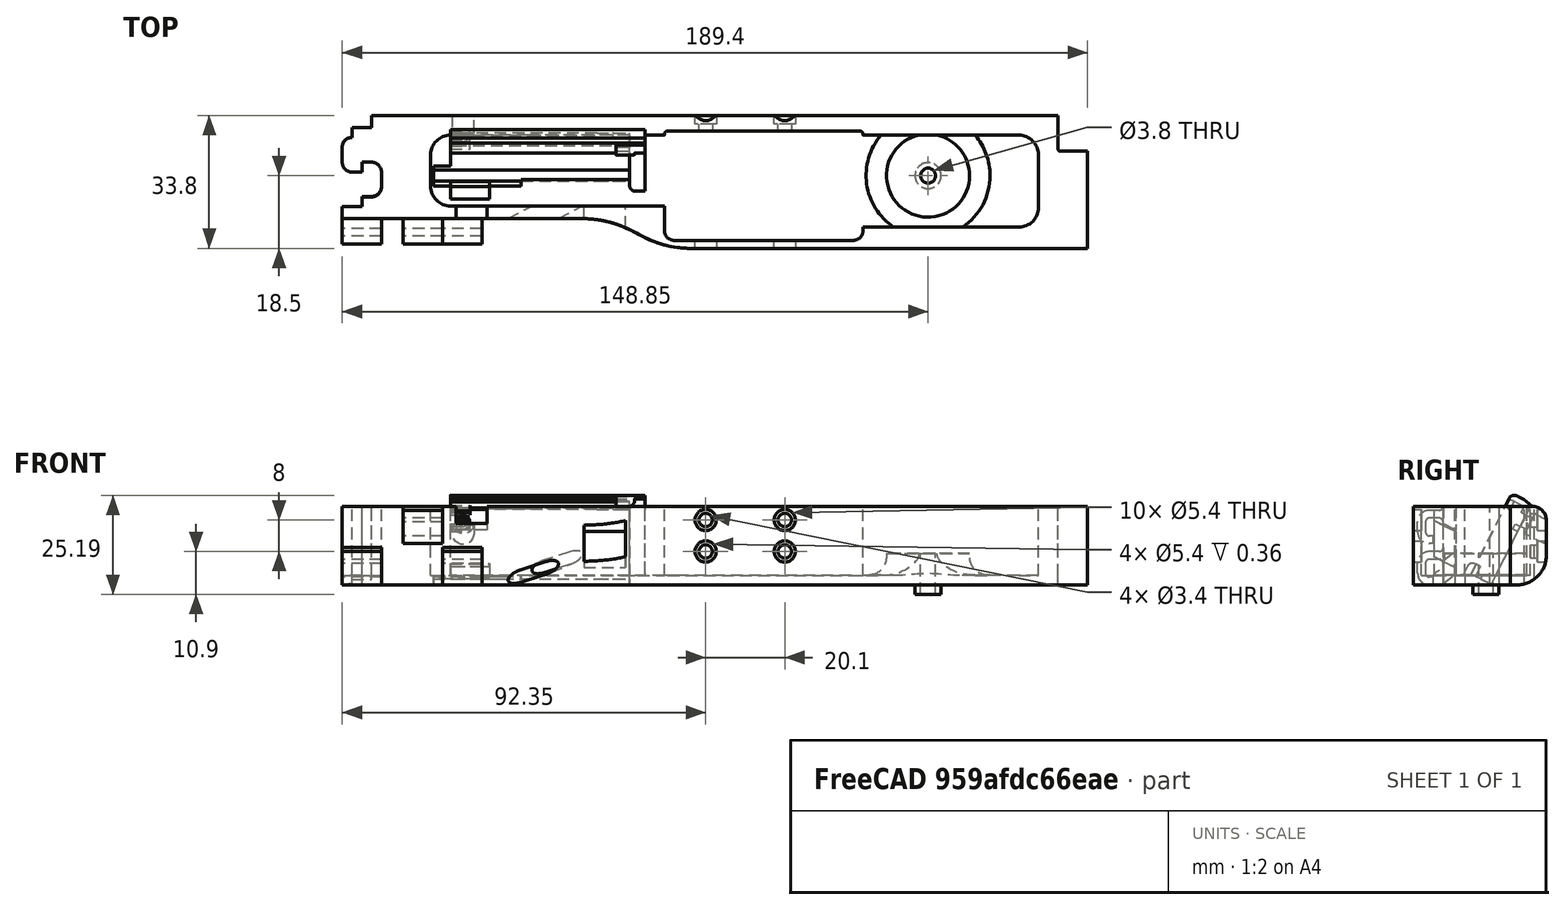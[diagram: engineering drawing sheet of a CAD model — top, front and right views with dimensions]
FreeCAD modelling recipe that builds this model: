
FCSTD DOCUMENT  (FreeCAD 0.19R0.19.2)
Label: v0_999
License: All rights reserved
LicenseURL: http://en.wikipedia.org/wiki/All_rights_reserved
objects: Sketcher::SketchObject×44, Part::Extrusion×34, Part::MultiFuse×19, Part::Cut×15, Part::Box×14, Part::Fillet×11, App::MeasureDistance×5, Part::Cylinder×4, Part::Revolution×1, Mesh::Feature×1
note: 142 computed .brp shape members not serialized (recipe doc carries the construction recipe); baked Part::Feature solids carry a one-line shape summary decoded from their .brp

FEATURE [Sketcher::SketchObject] Sketch
  FullyConstrained = true
  sketch-geometry (36):
    g0: LineSegment StartX=0 StartY=0 StartZ=0 EndX=154.4 EndY=0 EndZ=0
    g1: LineSegment StartX=154.4 StartY=0 StartZ=0 EndX=154.4 EndY=-7.6 EndZ=0
    g2: LineSegment StartX=32.5209 StartY=-26.2 StartZ=0 EndX=-7.5 EndY=-26.2 EndZ=0
    g3-g7: Circle x5 (B-spline internal-alignment scaffolding for g8; pole/knot coordinates omitted)
    g8: BSplineCurve PolesCount=5 KnotsCount=3 Degree=3 IsPeriodic=0
    g9: GeomPoint X=61.85 Y=-33.8 Z=0
    g10: GeomPoint X=47.185 Y=-29.9 Z=0
    g11: GeomPoint X=32.5209 Y=-26.2 Z=0
    g12: Circle CenterX=121.35 CenterY=-14.3 CenterZ=0 NormalX=0 NormalY=0 NormalZ=1 AngleXU=0 Radius=3.25
    g13: LineSegment StartX=-7.5 StartY=-26.2 StartZ=0 EndX=-27.5 EndY=-26.2 EndZ=0
    g14: LineSegment StartX=-20 StartY=0 StartZ=0 EndX=0 EndY=0 EndZ=0
    g15: LineSegment StartX=-25 StartY=-3.1 StartZ=0 EndX=-20 EndY=-3.1 EndZ=0
    g16: LineSegment StartX=-25 StartY=-3.1 StartZ=0 EndX=-25 EndY=-5.6 EndZ=0
    g17: LineSegment StartX=-27.5 StartY=-8.1 StartZ=0 EndX=-27.5 EndY=-11.85 EndZ=0
    g18: ArcOfCircle CenterX=-25 CenterY=-8.1 CenterZ=0 NormalX=0 NormalY=0 NormalZ=1 AngleXU=0 Radius=2.5 StartAngle=1.5708 EndAngle=3.14159
    g19: LineSegment StartX=-25 StartY=-14.35 StartZ=0 EndX=-22.5 EndY=-14.35 EndZ=0
    g20: ArcOfCircle CenterX=-25 CenterY=-11.85 CenterZ=0 NormalX=0 NormalY=0 NormalZ=1 AngleXU=0 Radius=2.5 StartAngle=3.14159 EndAngle=4.71239
    g21: LineSegment StartX=-22.5 StartY=-14.35 StartZ=0 EndX=-22.5 EndY=-11.85 EndZ=0
    g22: LineSegment StartX=-22.5 StartY=-11.85 StartZ=0 EndX=-20 EndY=-11.85 EndZ=0
    g23: ArcOfCircle CenterX=-20 CenterY=-14.35 CenterZ=0 NormalX=0 NormalY=0 NormalZ=1 AngleXU=0 Radius=2.5 StartAngle=8e-16 EndAngle=1.5708
    g24: LineSegment StartX=-17.5 StartY=-14.35 StartZ=0 EndX=-17.5 EndY=-18.1 EndZ=0
    g25: ArcOfCircle CenterX=-20 CenterY=-18.1 CenterZ=0 NormalX=0 NormalY=0 NormalZ=1 AngleXU=0 Radius=2.5 StartAngle=4.71239 EndAngle=6.28319
    g26: LineSegment StartX=-22.5 StartY=-20.6 StartZ=0 EndX=-20 EndY=-20.6 EndZ=0
    g27: LineSegment StartX=-22.5 StartY=-20.6 StartZ=0 EndX=-22.5 EndY=-23.1 EndZ=0
    g28: LineSegment StartX=-27.5 StartY=-23.1 StartZ=0 EndX=-22.5 EndY=-23.1 EndZ=0
    g29: LineSegment StartX=-20 StartY=-3.1 StartZ=0 EndX=-20 EndY=0 EndZ=0
    g30: LineSegment StartX=-27.5 StartY=-23.1 StartZ=0 EndX=-27.5 EndY=-26.2 EndZ=0
    g31: LineSegment StartX=154.4 StartY=-7.6 StartZ=0 EndX=154.4 EndY=-8.6 EndZ=0
    g32: ArcOfCircle CenterX=154.9 CenterY=-8.6 CenterZ=0 NormalX=0 NormalY=0 NormalZ=1 AngleXU=0 Radius=0.5 StartAngle=3.14159 EndAngle=4.71239
    g33: LineSegment StartX=154.9 StartY=-9.1 StartZ=0 EndX=161.9 EndY=-9.1 EndZ=0
    g34: LineSegment StartX=161.9 StartY=-9.1 StartZ=0 EndX=161.9 EndY=-33.8 EndZ=0
    g35: LineSegment StartX=161.9 StartY=-33.8 StartZ=0 EndX=61.85 EndY=-33.8 EndZ=0
  constraints (72):
    c: PointOnObject(g0,g-2)
    c: Horizontal(g0)
    c: Distance(g0) = 154.4
    c: DistanceY(g-1,g0) = 0
    c: Vertical(g1)
    c: Distance(g1) = 7.6
    c: Coincident(g1,g0)
    c: Horizontal(g2)
    c: Block(g2)
    c: Weight(g3) = 1
    c: Coincident(g8,g2)
    c: InternalAlignment(g3-g7 -> g8) x5
    c: InternalAlignment(g9,g8)
    c: InternalAlignment(g10,g8)
    c: InternalAlignment(g11,g8)
    c: Block(g12)
    c: Coincident(g13,g2)
    c: Horizontal(g13)
    c: Distance(g13) = 20
    c: Horizontal(g14)
    c: Distance(g14) = 20
    c: Coincident(g14,g0)
    c: Horizontal(g15)
    c: Vertical(g16)
    c: Coincident(g16,g15)
    c: Vertical(g17)
    c: Coincident(g18,g16)
    c: Block(g18)
    c: Coincident(g17,g18)
    c: Horizontal(g19)
    c: Coincident(g20,g17)
    c: Block(g20)
    c: Block(g19)
    c: Vertical(g21)
    c: Coincident(g21,g19)
    c: Horizontal(g22)
    c: Coincident(g22,g21)
    c: Coincident(g23,g22)
    c: Vertical(g24)
    c: Block(g23)
    c: Coincident(g24,g23)
    c: Coincident(g25,g24)
    c: Block(g25)
    c: Horizontal(g26)
    c: Coincident(g26,g25)
    c: Vertical(g27)
    c: Coincident(g27,g26)
    c: Horizontal(g28)
    c: Coincident(g28,g27)
    c: Block(g15)
    c: Block(g28)
    c: Coincident(g29,g15)
    c: Coincident(g29,g14)
    c: Vertical(g29)
    c: Coincident(g30,g28)
    c: Coincident(g30,g13)
    c: Vertical(g30)
    c: Vertical(g31)
    c: Distance(g31) = 1
    c: Coincident(g31,g1)
    c: Coincident(g32,g31)
    c: Block(g32)
    c: Coincident(g33,g32)
    c: Horizontal(g33)
    c: Coincident(g34,g33)
    c: Vertical(g34)
    c: Block(g34)
    c: Coincident(g35,g34)
    c: Horizontal(g35)
    c: Block(g35)
    c: Coincident(g8,g35)
    c: Block(g8)
FEATURE [Part::Extrusion] Extrude  label="mainBodyBaseExtrude"
  Base = -> Sketch
  Dir = (0,0,1)
  DirMode = 2
  FaceMakerClass = Part::FaceMakerBullseye
  LengthFwd = 2.4
  LengthRev = 0
  Solid = true
  Symmetric = false
FEATURE [Sketcher::SketchObject] Sketch001
  FullyConstrained = true
  sketch-geometry (75):
    g0: ArcOfCircle CenterX=144.4 CenterY=-10 CenterZ=0 NormalX=0 NormalY=0 NormalZ=1 AngleXU=0 Radius=5 StartAngle=4.345e-13 EndAngle=1.5708
    g1: LineSegment StartX=32.5209 StartY=-26.2 StartZ=0 EndX=-7.49911 EndY=-26.2 EndZ=0
    g2: LineSegment StartX=0 StartY=0 StartZ=0 EndX=154.4 EndY=0 EndZ=0
    g3-g7: Circle x5 (B-spline internal-alignment scaffolding for g8; pole/knot coordinates omitted)
    g8: BSplineCurve PolesCount=5 KnotsCount=3 Degree=3 IsPeriodic=0
    g9: GeomPoint X=61.85 Y=-33.8 Z=0
    g10: GeomPoint X=47.1857 Y=-29.9 Z=0
    g11: GeomPoint X=32.5209 Y=-26.2 Z=0
    g12: LineSegment StartX=154.4 StartY=0 StartZ=0 EndX=154.4 EndY=-7.6 EndZ=0
    g13: LineSegment StartX=20 StartY=-5 StartZ=0 EndX=54.35 EndY=-5 EndZ=0
    g14: LineSegment StartX=104.85 StartY=-5 StartZ=0 EndX=144.4 EndY=-5 EndZ=0
    g15: LineSegment StartX=54.35 StartY=-23 StartZ=0 EndX=20 EndY=-23 EndZ=0
    g16: LineSegment StartX=-27.4991 StartY=-26.2 StartZ=0 EndX=-7.49911 EndY=-26.2 EndZ=0
    g17: LineSegment StartX=-20 StartY=0 StartZ=0 EndX=0 EndY=0 EndZ=0
    g18: LineSegment StartX=-27.4991 StartY=-23.2 StartZ=0 EndX=-22.5 EndY=-23.2 EndZ=0
    g19: LineSegment StartX=-22.5 StartY=-20.7 StartZ=0 EndX=-22.5 EndY=-23.2 EndZ=0
    g20: LineSegment StartX=-22.5 StartY=-20.7 StartZ=0 EndX=-20 EndY=-20.7 EndZ=0
    g21: ArcOfCircle CenterX=-20 CenterY=-18.2 CenterZ=0 NormalX=0 NormalY=0 NormalZ=1 AngleXU=0 Radius=2.5 StartAngle=4.71239 EndAngle=6.28319
    g22: LineSegment StartX=-17.5 StartY=-14.4 StartZ=0 EndX=-17.5 EndY=-18.2 EndZ=0
    g23: ArcOfCircle CenterX=-20 CenterY=-14.4 CenterZ=0 NormalX=0 NormalY=0 NormalZ=1 AngleXU=0 Radius=2.5 StartAngle=9e-16 EndAngle=1.5708
    g24: LineSegment StartX=-22.5 StartY=-11.9 StartZ=0 EndX=-20 EndY=-11.9 EndZ=0
    g25: LineSegment StartX=-22.5 StartY=-14.4 StartZ=0 EndX=-22.5 EndY=-11.9 EndZ=0
    g26: LineSegment StartX=-25 StartY=-14.4 StartZ=0 EndX=-22.5 EndY=-14.4 EndZ=0
    g27: ArcOfCircle CenterX=-25 CenterY=-11.9 CenterZ=0 NormalX=0 NormalY=0 NormalZ=1 AngleXU=0 Radius=2.5 StartAngle=3.14159 EndAngle=4.71239
    g28: LineSegment StartX=-27.5 StartY=-8.1 StartZ=0 EndX=-27.5 EndY=-11.9 EndZ=0
    g29: ArcOfCircle CenterX=-25 CenterY=-8.1 CenterZ=0 NormalX=0 NormalY=0 NormalZ=1 AngleXU=0 Radius=2.5 StartAngle=1.5708 EndAngle=3.14159
    g30: LineSegment StartX=-25 StartY=-3.1 StartZ=0 EndX=-25 EndY=-5.6 EndZ=0
    g31: LineSegment StartX=-20 StartY=-3.1 StartZ=0 EndX=-25 EndY=-3.1 EndZ=0
    g32: LineSegment StartX=-20 StartY=0 StartZ=0 EndX=-20 EndY=-3.1 EndZ=0
    g33: LineSegment StartX=-27.4991 StartY=-26.2 StartZ=0 EndX=-27.4991 EndY=-23.2 EndZ=0
    g34: LineSegment StartX=4.09e-14 StartY=-5 StartZ=0 EndX=20 EndY=-5 EndZ=0
    g35: ArcOfCircle CenterX=7.1e-15 CenterY=-18 CenterZ=0 NormalX=0 NormalY=0 NormalZ=1 AngleXU=0 Radius=5 StartAngle=3.14159 EndAngle=4.71239
    g36: ArcOfCircle CenterX=4.26e-14 CenterY=-10 CenterZ=0 NormalX=0 NormalY=0 NormalZ=1 AngleXU=0 Radius=5 StartAngle=1.5708 EndAngle=3.14159
    g37: LineSegment StartX=-5 StartY=-18 StartZ=0 EndX=-5 EndY=-10 EndZ=0
    g38: LineSegment StartX=6.2e-15 StartY=-23 StartZ=0 EndX=20 EndY=-23 EndZ=0
    g39: LineSegment StartX=154.4 StartY=-7.6 StartZ=0 EndX=154.4 EndY=-8.6 EndZ=0
    g40: LineSegment StartX=154.9 StartY=-9.1 StartZ=0 EndX=161.9 EndY=-9.1 EndZ=0
    g41: ArcOfCircle CenterX=154.9 CenterY=-8.6 CenterZ=0 NormalX=0 NormalY=0 NormalZ=1 AngleXU=0 Radius=0.5 StartAngle=3.14159 EndAngle=4.71299
    g42: LineSegment StartX=104.85 StartY=-28.3916 StartZ=0 EndX=144.408 EndY=-28.3916 EndZ=0
    g43: LineSegment StartX=149.4 StartY=-10 StartZ=0 EndX=149.4 EndY=-23.4 EndZ=0
    g44: ArcOfCircle CenterX=144.408 CenterY=-23.4 CenterZ=0 NormalX=0 NormalY=0 NormalZ=1 AngleXU=0 Radius=4.99164 StartAngle=4.71239 EndAngle=6.28319
    g45: LineSegment StartX=104.85 StartY=-28.3916 StartZ=0 EndX=104.85 EndY=-28.7833 EndZ=0
    g46: LineSegment StartX=54.35 StartY=-28.7916 StartZ=0 EndX=54.35 EndY=-23 EndZ=0
    g47: LineSegment StartX=161.9 StartY=-33.8 StartZ=0 EndX=161.9 EndY=-9.1 EndZ=0
    g48: LineSegment StartX=61.85 StartY=-33.8 StartZ=0 EndX=161.9 EndY=-33.8 EndZ=0
    g49: Circle CenterX=54.35 CenterY=-28.7916 CenterZ=0 NormalX=0 NormalY=0 NormalZ=1 AngleXU=0 Radius=1
    g50: Circle CenterX=54.35 CenterY=-31.7916 CenterZ=0 NormalX=0 NormalY=0 NormalZ=1 AngleXU=0 Radius=1
    g51: Circle CenterX=57.35 CenterY=-31.7916 CenterZ=0 NormalX=0 NormalY=0 NormalZ=1 AngleXU=0 Radius=1
    g52: BSplineCurve PolesCount=3 KnotsCount=2 Degree=2 IsPeriodic=0
    g53: GeomPoint X=54.35 Y=-28.7916 Z=0
    g54: GeomPoint X=57.35 Y=-31.7916 Z=0
    g55: Circle CenterX=104.85 CenterY=-28.7833 CenterZ=0 NormalX=0 NormalY=0 NormalZ=1 AngleXU=0 Radius=1
    g56: Circle CenterX=104.85 CenterY=-31.7916 CenterZ=0 NormalX=0 NormalY=0 NormalZ=1 AngleXU=0 Radius=1
    g57: Circle CenterX=101.85 CenterY=-31.7916 CenterZ=0 NormalX=0 NormalY=0 NormalZ=1 AngleXU=0 Radius=1
    g58: BSplineCurve PolesCount=3 KnotsCount=2 Degree=2 IsPeriodic=0
    g59: GeomPoint X=104.85 Y=-28.7833 Z=0
    g60: GeomPoint X=101.85 Y=-31.7916 Z=0
    g61: LineSegment StartX=57.35 StartY=-31.7916 StartZ=0 EndX=101.85 EndY=-31.7916 EndZ=0
    g62: Circle CenterX=54.35 CenterY=-5 CenterZ=0 NormalX=0 NormalY=0 NormalZ=1 AngleXU=0 Radius=1
    g63: Circle CenterX=54.35 CenterY=-4 CenterZ=0 NormalX=0 NormalY=0 NormalZ=1 AngleXU=0 Radius=1
    g64: Circle CenterX=55.15 CenterY=-4 CenterZ=0 NormalX=0 NormalY=0 NormalZ=1 AngleXU=0 Radius=1
    g65: BSplineCurve PolesCount=3 KnotsCount=2 Degree=2 IsPeriodic=0
    g66: GeomPoint X=54.35 Y=-5 Z=0
    g67: GeomPoint X=55.15 Y=-4 Z=0
    g68: Circle CenterX=104.85 CenterY=-5 CenterZ=0 NormalX=0 NormalY=0 NormalZ=1 AngleXU=0 Radius=1
    g69: Circle CenterX=104.85 CenterY=-4 CenterZ=0 NormalX=0 NormalY=0 NormalZ=1 AngleXU=0 Radius=1
    g70: Circle CenterX=104.05 CenterY=-4 CenterZ=0 NormalX=0 NormalY=0 NormalZ=1 AngleXU=0 Radius=1
    g71: BSplineCurve PolesCount=3 KnotsCount=2 Degree=2 IsPeriodic=0
    g72: GeomPoint X=104.85 Y=-5 Z=0
    g73: GeomPoint X=104.05 Y=-4 Z=0
    g74: LineSegment StartX=104.05 StartY=-4 StartZ=0 EndX=55.15 EndY=-4 EndZ=0
  constraints (156):
    c: PointOnObject(g2,g-2)
    c: DistanceY(g-1,g2) = 0
    c: Block(g0)
    c: Horizontal(g1)
    c: Distance(g1) = 40.02
    c: Horizontal(g2)
    c: Block(g2)
    c: Weight(g3) = 1
    c: Equal(g3, g4-g7) x4
    c: Coincident(g8,g1)
    c: InternalAlignment(g3-g7 -> g8) x5
    c: InternalAlignment(g9,g8)
    c: InternalAlignment(g10,g8)
    c: InternalAlignment(g11,g8)
    c: Vertical(g12)
    c: Coincident(g12,g2)
    c: Distance(g12) = 7.6
    c: Block(g12)
    c: Horizontal(g13)
    c: Coincident(g14,g0)
    c: Horizontal(g14)
    c: Horizontal(g15)
    c: Horizontal(g16)
    c: Distance(g16) = 20
    c: Coincident(g1,g16)
    c: Horizontal(g17)
    c: Distance(g17) = 20
    c: Coincident(g17,g2)
    c: Horizontal(g31)
    c: Vertical(g30)
    c: Coincident(g29,g30)
    c: Vertical(g28)
    c: Block(g29)
    c: Coincident(g27,g28)
    c: Block(g27)
    c: Horizontal(g26)
    c: Coincident(g26,g27)
    c: Vertical(g25)
    c: Coincident(g25,g26)
    c: Horizontal(g24)
    c: Coincident(g23,g24)
    c: Block(g23)
    c: Vertical(g22)
    c: Coincident(g21,g22)
    c: Block(g21)
    c: Horizontal(g20)
    c: Coincident(g20,g21)
    c: Vertical(g19)
    c: Coincident(g19,g20)
    c: Horizontal(g18)
    c: Coincident(g18,g19)
    c: Coincident(g32,g17)
    c: Coincident(g32,g31)
    c: Vertical(g32)
    c: Coincident(g33,g16)
    c: Coincident(g33,g18)
    c: Vertical(g33)
    c: Block(g33)
    c: Block(g18)
    c: Block(g22)
    c: Block(g26)
    c: Block(g25)
    c: Block(g24)
    c: Block(g28)
    c: Block(g31)
    c: Block(g30)
    c: Horizontal(g34)
    c: Distance(g34) = 20
    c: Block(g35)
    c: Block(g36)
    c: Coincident(g37,g35)
    c: Coincident(g37,g36)
    c: Vertical(g37)
    c: Coincident(g38,g35)
    c: Coincident(g38,g15)
    c: Horizontal(g38)
    c: Block(g38)
    c: Block(g34)
    c: Block(g13)
    c: Vertical(g39)
    c: Distance(g39) = 1
    c: Coincident(g39,g12)
    c: Horizontal(g40)
    c: Coincident(g41,g39)
    c: Coincident(g41,g40)
    c: Block(g39)
    c: Block(g41)
    c: Horizontal(g42)
    c: Vertical(g43)
    c: Distance(g43) = 13.4
    c: Coincident(g43,g0)
    c: Block(g42)
    c: Block(g43)
    c: Coincident(g44,g43)
    c: Coincident(g44,g42)
    c: Block(g44)
    c: Distance(g15) = 34.35
    c: Coincident(g45,g42)
    c: Vertical(g45)
    c: Coincident(g46,g15)
    c: Vertical(g46)
    c: Coincident(g47,g40)
    c: Vertical(g47)
    c: Block(g47)
    c: Coincident(g48,g47)
    c: Horizontal(g48)
    c: Block(g48)
    c: Coincident(g8,g48)
    c: Block(g8)
    c: Coincident(g52,g46)
    c: Weight(g49) = 1
    c: Equal(g49,g50)
    c: Equal(g49,g51)
    c: InternalAlignment(g49,g52)
    c: InternalAlignment(g50,g52)
    c: InternalAlignment(g51,g52)
    c: InternalAlignment(g53,g52)
    c: InternalAlignment(g54,g52)
    c: Coincident(g58,g45)
    c: Weight(g55) = 1
    c: Equal(g55,g56)
    c: Equal(g55,g57)
    c: InternalAlignment(g55,g58)
    c: InternalAlignment(g56,g58)
    c: InternalAlignment(g57,g58)
    c: InternalAlignment(g59,g58)
    c: InternalAlignment(g60,g58)
    c: Block(g58)
    c: Block(g52)
    c: Coincident(g61,g52)
    c: Coincident(g61,g58)
    c: Horizontal(g61)
    c: Block(g14)
    c: Coincident(g65,g13)
    c: Weight(g62) = 1
    c: Equal(g62,g63)
    c: Equal(g62,g64)
    c: InternalAlignment(g62,g65)
    c: InternalAlignment(g63,g65)
    c: InternalAlignment(g64,g65)
    c: InternalAlignment(g66,g65)
    c: InternalAlignment(g67,g65)
    c: Block(g65)
    c: Coincident(g71,g14)
    c: Weight(g68) = 1
    c: Equal(g68,g69)
    c: Equal(g68,g70)
    c: InternalAlignment(g68,g71)
    c: InternalAlignment(g69,g71)
    c: InternalAlignment(g70,g71)
    c: InternalAlignment(g72,g71)
    c: InternalAlignment(g73,g71)
    c: Block(g71)
    c: Coincident(g74,g71)
    c: Coincident(g74,g65)
    c: Horizontal(g74)
FEATURE [Sketcher::SketchObject] Sketch005
  FullyConstrained = true
  Placement = pos=(0,0,0) rot=(1,0,0;1.5708rad)
  sketch-geometry (4):
    g0: Circle CenterX=84.95 CenterY=16.5 CenterZ=0 NormalX=0 NormalY=0 NormalZ=1 AngleXU=0 Radius=1.7
    g1: Circle CenterX=84.95 CenterY=8.5 CenterZ=0 NormalX=0 NormalY=0 NormalZ=1 AngleXU=0 Radius=1.7
    g2: Circle CenterX=64.85 CenterY=8.5 CenterZ=0 NormalX=0 NormalY=0 NormalZ=1 AngleXU=0 Radius=1.7
    g3: Circle CenterX=64.85 CenterY=16.5 CenterZ=0 NormalX=0 NormalY=0 NormalZ=1 AngleXU=0 Radius=1.7
  constraints (4):
    c: Block(g0)
    c: Block(g1)
    c: Block(g2)
    c: Block(g3)
FEATURE [Part::Extrusion] Extrude004  label="removeFromMainBodyToCreateScrewHolesForSolenoidExtrude004"
  Base = -> Sketch005
  Dir = (0,-1,1.1e-15)
  DirMode = 2
  FaceMakerClass = Part::FaceMakerBullseye
  LengthFwd = 10
  LengthRev = 0
  Solid = true
  Symmetric = false
FEATURE [Sketcher::SketchObject] Sketch004
  FullyConstrained = true
  Placement = pos=(0,0,0) rot=(1,0,0;1.5708rad)
  sketch-geometry (12):
    g0: LineSegment StartX=15.75 StartY=2.5 StartZ=0 EndX=15.75 EndY=0 EndZ=0
    g1: Circle CenterX=15.75 CenterY=2.5 CenterZ=0 NormalX=0 NormalY=0 NormalZ=1 AngleXU=0 Radius=1
    g2: Circle CenterX=10.55 CenterY=2.5 CenterZ=0 NormalX=0 NormalY=0 NormalZ=1 AngleXU=0 Radius=1
    g3: Circle CenterX=10.55 CenterY=8 CenterZ=0 NormalX=0 NormalY=0 NormalZ=1 AngleXU=0 Radius=1
    g4: BSplineCurve PolesCount=3 KnotsCount=2 Degree=2 IsPeriodic=0
    g5: GeomPoint X=15.75 Y=2.5 Z=0
    g6: GeomPoint X=10.55 Y=8 Z=0
    g7: LineSegment StartX=1.9 StartY=8 StartZ=0 EndX=10.55 EndY=8 EndZ=0
    g8: LineSegment StartX=1.9 StartY=-2.4 StartZ=0 EndX=1.9 EndY=8 EndZ=0
    g9: LineSegment StartX=3.30092 StartY=-2.4 StartZ=0 EndX=3.30092 EndY=0 EndZ=0
    g10: LineSegment StartX=15.75 StartY=0 StartZ=0 EndX=3.30092 EndY=0 EndZ=0
    g11: LineSegment StartX=3.30092 StartY=-2.4 StartZ=0 EndX=1.9 EndY=-2.4 EndZ=0
  constraints (26):
    c: Vertical(g0)
    c: Distance(g0) = 2.5
    c: Coincident(g4,g0)
    c: Weight(g1) = 1
    c: Equal(g1,g2)
    c: Equal(g1,g3)
    c: InternalAlignment(g1,g4)
    c: InternalAlignment(g2,g4)
    c: InternalAlignment(g3,g4)
    c: InternalAlignment(g5,g4)
    c: InternalAlignment(g6,g4)
    c: Block(g4)
    c: Coincident(g7,g4)
    c: Horizontal(g7)
    c: Vertical(g8)
    c: Coincident(g8,g7)
    c: Block(g8)
    c: Vertical(g9)
    c: Coincident(g10,g0)
    c: PointOnObject(g10,g-1)
    c: Horizontal(g10)
    c: Coincident(g10,g9)
    c: Block(g9)
    c: Coincident(g11,g9)
    c: Coincident(g11,g8)
    c: Horizontal(g11)
FEATURE [Sketcher::SketchObject] Sketch007
  FullyConstrained = true
  Placement = pos=(0,-14.3,2.37) rot=(-1,0,0;2.03453rad)
  sketch-geometry (6):
    g0: LineSegment StartX=0 StartY=0 StartZ=0 EndX=45.5 EndY=0 EndZ=0
    g1: LineSegment StartX=0 StartY=0 StartZ=0 EndX=0 EndY=-21.2 EndZ=0
    g2: LineSegment StartX=45.5 StartY=0 StartZ=0 EndX=49.5 EndY=0 EndZ=0
    g3: LineSegment StartX=49.5 StartY=0 StartZ=0 EndX=49.5 EndY=-21.2 EndZ=0
    g4: LineSegment StartX=49.5 StartY=-21.2 StartZ=0 EndX=0 EndY=-21.2 EndZ=0
    g5: Circle CenterX=3.25 CenterY=-18.05 CenterZ=0 NormalX=0 NormalY=0 NormalZ=1 AngleXU=0 Radius=1.6
  constraints (15):
    c: Coincident(g0,g-1)
    c: Horizontal(g0)
    c: Distance(g0) = 45.5
    c: Coincident(g1,g0)
    c: Vertical(g1)
    c: Horizontal(g2)
    c: Distance(g2) = 4
    c: Coincident(g2,g0)
    c: Coincident(g3,g2)
    c: Vertical(g3)
    c: Block(g3)
    c: Coincident(g4,g3)
    c: Horizontal(g4)
    c: Coincident(g4,g1)
    c: Block(g5)
FEATURE [Part::Extrusion] Extrude005  label="solenoidDriverHolderExtrude005"
  Base = -> Sketch007
  Dir = (0,0.894389,-0.447291)
  DirMode = 2
  FaceMakerClass = Part::FaceMakerBullseye
  LengthFwd = 10
  LengthRev = 0
  Placement = pos=(0,0,-2) rot=(0,0,1;0rad)
  Solid = true
  Symmetric = false
FEATURE [Sketcher::SketchObject] Sketch008
  FullyConstrained = false
  Placement = pos=(0,-4.3,-2.6) rot=(-1,0,0;2.03453rad)
  sketch-geometry (1):
    g0: Circle CenterX=42.25 CenterY=-3.15 CenterZ=0 NormalX=0 NormalY=0 NormalZ=1 AngleXU=0 Radius=4.5
FEATURE [Sketcher::SketchObject] Sketch009
  FullyConstrained = true
  Placement = pos=(0,-4.3,-2.6) rot=(-1,0,0;2.03453rad)
  sketch-geometry (1):
    g0: Circle CenterX=3.25 CenterY=-18.0217 CenterZ=0 NormalX=0 NormalY=0 NormalZ=1 AngleXU=0 Radius=2.8
  constraints (1):
    c: Block(g0)
FEATURE [Sketcher::SketchObject] Sketch010
  FullyConstrained = true
  Placement = pos=(0,-14.3,2.37) rot=(-1,0,0;2.03453rad)
  sketch-geometry (1):
    g0: Circle CenterX=3.25 CenterY=-18.05 CenterZ=0 NormalX=0 NormalY=0 NormalZ=1 AngleXU=0 Radius=1.6
  constraints (1):
    c: Block(g0)
FEATURE [Part::Extrusion] Extrude008  label="removeFromScrewHole3"
  Base = -> Sketch010
  Dir = (0,0.894389,-0.447291)
  DirMode = 2
  FaceMakerClass = Part::FaceMakerBullseye
  LengthFwd = -25
  LengthRev = 0
  Placement = pos=(0,4,-4) rot=(0,0,1;0rad)
  Solid = true
  Symmetric = false
FEATURE [Sketcher::SketchObject] Sketch011
  FullyConstrained = true
  Placement = pos=(0,-14.3,2.37) rot=(-1,0,0;2.03453rad)
  sketch-geometry (4):
    g0: LineSegment StartX=49.5 StartY=-21.2 StartZ=0 EndX=49.5 EndY=-22.8 EndZ=0
    g1: LineSegment StartX=49.5 StartY=-22.8 StartZ=0 EndX=0.002238 EndY=-22.8 EndZ=0
    g2: LineSegment StartX=0.002238 StartY=-21.2 StartZ=0 EndX=0.002238 EndY=-22.8 EndZ=0
    g3: LineSegment StartX=49.5 StartY=-21.2 StartZ=0 EndX=0.002238 EndY=-21.2 EndZ=0
  constraints (10):
    c: Vertical(g0)
    c: Distance(g0) = 1.6
    c: Coincident(g1,g0)
    c: Horizontal(g1)
    c: Vertical(g2)
    c: Coincident(g2,g1)
    c: Coincident(g3,g0)
    c: Coincident(g3,g2)
    c: Horizontal(g3)
    c: Block(g3)
FEATURE [Part::Extrusion] Extrude009  label="solenoidDriverTopLipFront"
  Base = -> Sketch011
  Dir = (0,0.894389,-0.447291)
  DirMode = 2
  FaceMakerClass = Part::FaceMakerBullseye
  LengthFwd = -2
  LengthRev = 0
  Placement = pos=(0,-2.9,-0.35) rot=(0,0,1;0rad)
  Solid = true
  Symmetric = false
FEATURE [Sketcher::SketchObject] Sketch012
  FullyConstrained = true
  Placement = pos=(0,-14.3,2.37) rot=(-1,0,0;2.03453rad)
  sketch-geometry (4):
    g0: LineSegment StartX=49.5 StartY=-21.2 StartZ=0 EndX=49.5 EndY=-22.8 EndZ=0
    g1: LineSegment StartX=49.5 StartY=-22.8 StartZ=0 EndX=0.002238 EndY=-22.8 EndZ=0
    g2: LineSegment StartX=0.002238 StartY=-21.2 StartZ=0 EndX=0.002238 EndY=-22.8 EndZ=0
    g3: LineSegment StartX=49.5 StartY=-21.2 StartZ=0 EndX=0.002238 EndY=-21.2 EndZ=0
  constraints (10):
    c: Vertical(g0)
    c: Distance(g0) = 1.6
    c: Coincident(g1,g0)
    c: Horizontal(g1)
    c: Vertical(g2)
    c: Coincident(g2,g1)
    c: Coincident(g3,g0)
    c: Coincident(g3,g2)
    c: Horizontal(g3)
    c: Block(g3)
FEATURE [Part::Extrusion] Extrude010  label="solenoidDriverTopLipLowerExtrude010"
  Base = -> Sketch012
  Dir = (0,0.894389,-0.447291)
  DirMode = 2
  FaceMakerClass = Part::FaceMakerBullseye
  LengthFwd = 5.05
  LengthRev = 0
  Solid = true
  Symmetric = false
FEATURE [Sketcher::SketchObject] Sketch015
  FullyConstrained = true
  Placement = pos=(0,-14.3,2.37) rot=(-1,0,0;2.03453rad)
  sketch-geometry (4):
    g0: LineSegment StartX=0 StartY=1.5 StartZ=0 EndX=0 EndY=0 EndZ=0
    g1: LineSegment StartX=0 StartY=1.5 StartZ=0 EndX=5 EndY=1.5 EndZ=0
    g2: LineSegment StartX=5 StartY=1.5 StartZ=0 EndX=5 EndY=0 EndZ=0
    g3: LineSegment StartX=0 StartY=0 StartZ=0 EndX=5 EndY=0 EndZ=0
  constraints (13):
    c: Vertical(g0)
    c: Distance(g0) = 1.5
    c: Horizontal(g1)
    c: Distance(g1) = 5
    c: Coincident(g1,g0)
    c: Vertical(g2)
    c: Distance(g2) = 1.5
    c: Coincident(g2,g1)
    c: Block(g1)
    c: Block(g2)
    c: Block(g0)
    c: Coincident(g3,g0)
    c: Coincident(g3,g2)
FEATURE [Part::Extrusion] Extrude013  label="solenoidDriverBottomLipTopExtrude012"
  Base = -> Sketch015
  Dir = (0,0.894389,-0.447291)
  DirMode = 2
  FaceMakerClass = Part::FaceMakerBullseye
  LengthFwd = -6.5
  LengthRev = 0
  Placement = pos=(0,-14.15,19.65) rot=(1,0,0;1.5708rad)
  Solid = true
  Symmetric = false
FEATURE [Sketcher::SketchObject] Sketch016
  FullyConstrained = true
  Placement = pos=(0,0,0) rot=(1,0,0;1.5708rad)
  sketch-geometry (4):
    g0: Circle CenterX=84.15 CenterY=16.5 CenterZ=0 NormalX=0 NormalY=0 NormalZ=1 AngleXU=0 Radius=2.7
    g1: Circle CenterX=64.05 CenterY=16.5 CenterZ=0 NormalX=0 NormalY=0 NormalZ=1 AngleXU=0 Radius=2.7
    g2: Circle CenterX=64.05 CenterY=8.5 CenterZ=0 NormalX=0 NormalY=0 NormalZ=1 AngleXU=0 Radius=2.7
    g3: Circle CenterX=84.15 CenterY=8.5 CenterZ=0 NormalX=0 NormalY=0 NormalZ=1 AngleXU=0 Radius=2.7
  constraints (4):
    c: Block(g0)
    c: Block(g1)
    c: Block(g3)
    c: Block(g2)
FEATURE [Part::Extrusion] Extrude014  label="removeFromMainBodyToCreateScrewHoleCounterSinks"
  Base = -> Sketch016
  Dir = (0,-1,1.1e-15)
  DirMode = 2
  FaceMakerClass = Part::FaceMakerBullseye
  LengthFwd = 1.9
  LengthRev = 0
  Placement = pos=(0.8,-0.36,0) rot=(0,0,1;0rad)
  Solid = true
  Symmetric = false
FEATURE [Part::Extrusion] Extrude015  label="removeFromScrewHole2Extrude007"
  Base = -> Sketch009
  Dir = (0,0.894389,-0.447291)
  DirMode = 2
  FaceMakerClass = Part::FaceMakerBullseye
  LengthFwd = 10
  LengthRev = 0
  Placement = pos=(0,-8,2) rot=(0,0,1;0rad)
  Solid = true
  Symmetric = false
FEATURE [Sketcher::SketchObject] Sketch017
  FullyConstrained = true
  Placement = pos=(0,-14.3,2.37) rot=(-1,0,0;2.03453rad)
  sketch-geometry (4):
    g0: LineSegment StartX=0 StartY=1.5 StartZ=0 EndX=0 EndY=0 EndZ=0
    g1: LineSegment StartX=0 StartY=1.5 StartZ=0 EndX=5 EndY=1.5 EndZ=0
    g2: LineSegment StartX=5 StartY=1.5 StartZ=0 EndX=5 EndY=0 EndZ=0
    g3: LineSegment StartX=0 StartY=0 StartZ=0 EndX=5 EndY=0 EndZ=0
  constraints (13):
    c: Vertical(g0)
    c: Distance(g0) = 1.5
    c: Horizontal(g1)
    c: Distance(g1) = 5
    c: Coincident(g1,g0)
    c: Vertical(g2)
    c: Distance(g2) = 1.5
    c: Coincident(g2,g1)
    c: Block(g1)
    c: Block(g2)
    c: Block(g0)
    c: Coincident(g3,g0)
    c: Coincident(g3,g2)
FEATURE [Part::Extrusion] Extrude016  label="solenoidDriverBottomLipTopExtrude013"
  Base = -> Sketch017
  Dir = (0,0.894389,-0.447291)
  DirMode = 2
  FaceMakerClass = Part::FaceMakerBullseye
  LengthFwd = -6.5
  LengthRev = 0
  Placement = pos=(0,-15.45,20.3) rot=(1,0,0;1.5708rad)
  Solid = true
  Symmetric = false
FEATURE [Part::Fillet] Fillet005  label="solenoidDriverBottomLipTopFillet005"
  Base = -> Extrude016
  Edges = 1 edges r=1.4: [Edge6]
FEATURE [Sketcher::SketchObject] Sketch018
  FullyConstrained = true
  Placement = pos=(38.5,-14.3,2.37) rot=(-1,0,0;2.03453rad)
  sketch-geometry (4):
    g0: LineSegment StartX=11 StartY=0 StartZ=0 EndX=11 EndY=1.5 EndZ=0
    g1: LineSegment StartX=11 StartY=0 StartZ=0 EndX=3.6 EndY=0 EndZ=0
    g2: LineSegment StartX=3.6 StartY=0 StartZ=0 EndX=3.6 EndY=1.5 EndZ=0
    g3: LineSegment StartX=11 StartY=1.5 StartZ=0 EndX=3.6 EndY=1.5 EndZ=0
  constraints (12):
    c: PointOnObject(g0,g-1)
    c: Vertical(g0)
    c: Distance(g0) = 1.5
    c: Horizontal(g1)
    c: Distance(g1) = 7.4
    c: Coincident(g1,g0)
    c: Block(g0)
    c: Coincident(g2,g1)
    c: Vertical(g2)
    c: Coincident(g3,g0)
    c: Horizontal(g3)
    c: Coincident(g2,g3)
FEATURE [Part::Extrusion] Extrude017
  Base = -> Sketch018
  Dir = (0,0.894389,-0.447291)
  DirMode = 2
  FaceMakerClass = Part::FaceMakerBullseye
  LengthFwd = 4
  LengthRev = 0
  Placement = pos=(0,-8.212,34.025) rot=(1,0,0;1.5708rad)
  Solid = true
  Symmetric = false
FEATURE [Sketcher::SketchObject] Sketch019
  FullyConstrained = true
  Placement = pos=(0,0,0) rot=(1,0,0;1.5708rad)
  sketch-geometry (4):
    g0: Circle CenterX=84.95 CenterY=8.5 CenterZ=0 NormalX=0 NormalY=0 NormalZ=1 AngleXU=0 Radius=2.7
    g1: Circle CenterX=64.85 CenterY=8.5 CenterZ=0 NormalX=0 NormalY=0 NormalZ=1 AngleXU=0 Radius=2.7
    g2: Circle CenterX=64.85 CenterY=16.5 CenterZ=0 NormalX=0 NormalY=0 NormalZ=1 AngleXU=0 Radius=2.7
    g3: Circle CenterX=84.95 CenterY=16.5 CenterZ=0 NormalX=0 NormalY=0 NormalZ=1 AngleXU=0 Radius=2.7
  constraints (4):
    c: Block(g3)
    c: Block(g2)
    c: Block(g0)
    c: Block(g1)
FEATURE [Part::Extrusion] Extrude019  label="removeSolenoidAdjusterHoles"
  Base = -> Sketch019
  Dir = (0,-1,1.1e-15)
  DirMode = 2
  FaceMakerClass = Part::FaceMakerBullseye
  LengthFwd = 6
  LengthRev = 0
  Placement = pos=(0,-30,0) rot=(0,0,1;0rad)
  Solid = true
  Symmetric = false
FEATURE [Sketcher::SketchObject] Sketch020
  FullyConstrained = true
  Placement = pos=(0,-14.3,2.37) rot=(-1,0,0;2.03453rad)
  sketch-geometry (6):
    g0: LineSegment StartX=45.5 StartY=-21.2 StartZ=0 EndX=49.5 EndY=-21.2 EndZ=0
    g1: LineSegment StartX=45.5 StartY=0 StartZ=0 EndX=49.5 EndY=0 EndZ=0
    g2: LineSegment StartX=49.5 StartY=0 StartZ=0 EndX=49.5 EndY=-21.2 EndZ=0
    g3: LineSegment StartX=4 StartY=0 StartZ=0 EndX=4 EndY=-21.2 EndZ=0
    g4: LineSegment StartX=45.5 StartY=-21.2 StartZ=0 EndX=4 EndY=-21.2 EndZ=0
    g5: LineSegment StartX=4 StartY=0 StartZ=0 EndX=45.5 EndY=0 EndZ=0
  constraints (16):
    c: Horizontal(g0)
    c: Distance(g0) = 4
    c: Horizontal(g1)
    c: Distance(g1) = 4
    c: Coincident(g2,g1)
    c: Coincident(g2,g0)
    c: Vertical(g2)
    c: Block(g2)
    c: Vertical(g3)
    c: Coincident(g4,g0)
    c: Horizontal(g4)
    c: Coincident(g4,g3)
    c: Coincident(g5,g1)
    c: Horizontal(g5)
    c: Block(g3)
    c: Block(g5)
FEATURE [Part::Box] Box  label="Cube"
  AttacherType = Attacher::AttachEngine3D
  Height = 10
  Length = 190
  Placement = pos=(-30,0,0) rot=(0,0,1;0rad)
  Width = 10
FEATURE [Part::Fillet] Fillet008
  Base = -> Box
  Edges = 1 edges r=7.5: [Edge11]
FEATURE [Part::Box] Box001  label="Cube001"
  AttacherType = Attacher::AttachEngine3D
  Height = 10
  Length = 190
  Placement = pos=(-35,0,0) rot=(0,0,1;0rad)
  Width = 10
FEATURE [Part::Cut] Cut  label="filletMain"
  Base = -> Box001
  Placement = pos=(0,-10,0) rot=(0,0,1;0rad)
  Tool = -> Fillet008
FEATURE [Part::Box] Box002  label="Cube002"
  AttacherType = Attacher::AttachEngine3D
  Height = 30
  Length = 190
  Placement = pos=(-20,0,0) rot=(0,0,1;0rad)
  Width = 10
FEATURE [Part::Box] Box003  label="Cube003"
  AttacherType = Attacher::AttachEngine3D
  Height = 10
  Length = 190
  Placement = pos=(-90,-50,-10) rot=(0,0,1;0rad)
  Width = 50
FEATURE [Sketcher::SketchObject] Sketch021
  FullyConstrained = true
  Placement = pos=(0,-14.3,2.37) rot=(-1,0,0;2.03453rad)
  sketch-geometry (6):
    g0: LineSegment StartX=41.65 StartY=-3.15 StartZ=0 EndX=38.95 EndY=-3.15 EndZ=0
    g1: LineSegment StartX=36.25 StartY=-3.15 StartZ=0 EndX=38.95 EndY=-3.15 EndZ=0
    g2: LineSegment StartX=41.65 StartY=-3.15 StartZ=0 EndX=41.65 EndY=-7.15 EndZ=0
    g3: LineSegment StartX=38.95 StartY=-7.15 StartZ=0 EndX=41.65 EndY=-7.15 EndZ=0
    g4: LineSegment StartX=38.95 StartY=-7.15 StartZ=0 EndX=36.25 EndY=-7.15 EndZ=0
    g5: LineSegment StartX=36.25 StartY=-3.15 StartZ=0 EndX=36.25 EndY=-7.15 EndZ=0
  constraints (16):
    c: Horizontal(g0)
    c: Distance(g0) = 2.7
    c: Horizontal(g1)
    c: Distance(g1) = 2.7
    c: Coincident(g1,g0)
    c: Block(g0)
    c: Coincident(g2,g0)
    c: Vertical(g2)
    c: Horizontal(g3)
    c: Coincident(g3,g2)
    c: Horizontal(g4)
    c: Coincident(g5,g1)
    c: Vertical(g5)
    c: Coincident(g5,g4)
    c: Block(g3)
    c: Block(g4)
FEATURE [Sketcher::SketchObject] Sketch022
  FullyConstrained = true
  Placement = pos=(0,-14.3,2.37) rot=(-1,0,0;2.03453rad)
  sketch-geometry (6):
    g0: LineSegment StartX=41.65 StartY=-3.15 StartZ=0 EndX=38.95 EndY=-3.15 EndZ=0
    g1: LineSegment StartX=36.25 StartY=-3.15 StartZ=0 EndX=38.95 EndY=-3.15 EndZ=0
    g2: LineSegment StartX=41.65 StartY=-3.15 StartZ=0 EndX=41.65 EndY=-7.15 EndZ=0
    g3: LineSegment StartX=38.95 StartY=-7.15 StartZ=0 EndX=41.65 EndY=-7.15 EndZ=0
    g4: LineSegment StartX=38.95 StartY=-7.15 StartZ=0 EndX=36.25 EndY=-7.15 EndZ=0
    g5: LineSegment StartX=36.25 StartY=-3.15 StartZ=0 EndX=36.25 EndY=-7.15 EndZ=0
  constraints (16):
    c: Horizontal(g0)
    c: Distance(g0) = 2.7
    c: Horizontal(g1)
    c: Distance(g1) = 2.7
    c: Coincident(g1,g0)
    c: Block(g0)
    c: Coincident(g2,g0)
    c: Vertical(g2)
    c: Horizontal(g3)
    c: Coincident(g3,g2)
    c: Horizontal(g4)
    c: Coincident(g5,g1)
    c: Vertical(g5)
    c: Coincident(g5,g4)
    c: Block(g3)
    c: Block(g4)
FEATURE [Sketcher::SketchObject] Sketch024
  FullyConstrained = true
  Placement = pos=(0,-14.3,2.37) rot=(-1,0,0;2.03453rad)
  sketch-geometry (4):
    g0: LineSegment StartX=49.5 StartY=-21.2 StartZ=0 EndX=49.5 EndY=-22.8 EndZ=0
    g1: LineSegment StartX=49.5 StartY=-22.8 StartZ=0 EndX=0.002238 EndY=-22.8 EndZ=0
    g2: LineSegment StartX=0.002238 StartY=-21.2 StartZ=0 EndX=0.002238 EndY=-22.8 EndZ=0
    g3: LineSegment StartX=49.5 StartY=-21.2 StartZ=0 EndX=0.002238 EndY=-21.2 EndZ=0
  constraints (10):
    c: Vertical(g0)
    c: Distance(g0) = 1.6
    c: Coincident(g1,g0)
    c: Horizontal(g1)
    c: Vertical(g2)
    c: Coincident(g2,g1)
    c: Coincident(g3,g0)
    c: Coincident(g3,g2)
    c: Horizontal(g3)
    c: Block(g3)
FEATURE [Sketcher::SketchObject] Sketch025
  FullyConstrained = true
  Placement = pos=(0,-14.3,2.37) rot=(-1,0,0;2.03453rad)
  sketch-geometry (4):
    g0: LineSegment StartX=0 StartY=1.5 StartZ=0 EndX=0 EndY=0 EndZ=0
    g1: LineSegment StartX=0 StartY=1.5 StartZ=0 EndX=5 EndY=1.5 EndZ=0
    g2: LineSegment StartX=5 StartY=1.5 StartZ=0 EndX=5 EndY=0 EndZ=0
    g3: LineSegment StartX=0 StartY=0 StartZ=0 EndX=5 EndY=0 EndZ=0
  constraints (13):
    c: Vertical(g0)
    c: Distance(g0) = 1.5
    c: Horizontal(g1)
    c: Distance(g1) = 5
    c: Coincident(g1,g0)
    c: Vertical(g2)
    c: Distance(g2) = 1.5
    c: Coincident(g2,g1)
    c: Block(g1)
    c: Block(g2)
    c: Block(g0)
    c: Coincident(g3,g0)
    c: Coincident(g3,g2)
FEATURE [Part::Extrusion] Extrude022  label="solenoidDriverBottomLipTopExtrude014"
  Base = -> Sketch025
  Dir = (0,0.894389,-0.447291)
  DirMode = 2
  FaceMakerClass = Part::FaceMakerBullseye
  LengthFwd = -6.5
  LengthRev = 0
  Placement = pos=(0,-15.45,20.3) rot=(1,0,0;1.5708rad)
  Solid = true
  Symmetric = false
FEATURE [Part::Fillet] Fillet013  label="solenoidDriverBottomLipTopFillet006"
  Base = -> Extrude022
  Edges = 1 edges r=1.4: [Edge6]
  Placement = pos=(5,0,0) rot=(0,0,1;0rad)
FEATURE [Sketcher::SketchObject] Sketch026
  FullyConstrained = true
  Placement = pos=(0,-14.3,2.37) rot=(-1,0,0;2.03453rad)
  sketch-geometry (4):
    g0: LineSegment StartX=0 StartY=1.5 StartZ=0 EndX=0 EndY=0 EndZ=0
    g1: LineSegment StartX=0 StartY=1.5 StartZ=0 EndX=5 EndY=1.5 EndZ=0
    g2: LineSegment StartX=5 StartY=1.5 StartZ=0 EndX=5 EndY=0 EndZ=0
    g3: LineSegment StartX=0 StartY=0 StartZ=0 EndX=5 EndY=0 EndZ=0
  constraints (13):
    c: Vertical(g0)
    c: Distance(g0) = 1.5
    c: Horizontal(g1)
    c: Distance(g1) = 5
    c: Coincident(g1,g0)
    c: Vertical(g2)
    c: Distance(g2) = 1.5
    c: Coincident(g2,g1)
    c: Block(g1)
    c: Block(g2)
    c: Block(g0)
    c: Coincident(g3,g0)
    c: Coincident(g3,g2)
FEATURE [Part::Extrusion] Extrude023  label="solenoidDriverBottomLipTopExtrude015"
  Base = -> Sketch026
  Dir = (0,0.894389,-0.447291)
  DirMode = 2
  FaceMakerClass = Part::FaceMakerBullseye
  LengthFwd = -6.5
  LengthRev = 0
  Placement = pos=(5,-14.15,19.65) rot=(1,0,0;1.5708rad)
  Solid = true
  Symmetric = false
FEATURE [Sketcher::SketchObject] Sketch027
  FullyConstrained = true
  Placement = pos=(0,-14.3,2.37) rot=(-1,0,0;2.03453rad)
  sketch-geometry (5):
    g0: LineSegment StartX=45.5 StartY=-21.2 StartZ=0 EndX=49.5 EndY=-21.2 EndZ=0
    g1: LineSegment StartX=49.5 StartY=0 StartZ=0 EndX=49.5 EndY=-21.2 EndZ=0
    g2: LineSegment StartX=49.5 StartY=0 StartZ=0 EndX=49.5 EndY=1.6 EndZ=0
    g3: LineSegment StartX=45.5 StartY=-21.2 StartZ=0 EndX=45.5 EndY=1.6 EndZ=0
    g4: LineSegment StartX=49.5 StartY=1.6 StartZ=0 EndX=45.5 EndY=1.6 EndZ=0
  constraints (14):
    c: Horizontal(g0)
    c: Distance(g0) = 4
    c: Coincident(g1,g0)
    c: Vertical(g1)
    c: Block(g1)
    c: Vertical(g2)
    c: Distance(g2) = 1.6
    c: Block(g2)
    c: Coincident(g3,g0)
    c: Vertical(g3)
    c: Coincident(g4,g2)
    c: Horizontal(g4)
    c: Block(g0)
    c: Coincident(g3,g4)
FEATURE [Part::Extrusion] Extrude024
  Base = -> Sketch027
  Dir = (0,0.894389,-0.447291)
  DirMode = 2
  FaceMakerClass = Part::FaceMakerBullseye
  LengthFwd = 6.34
  LengthRev = 0
  Placement = pos=(0,-5.59,1) rot=(0,0,1;0rad)
  Solid = true
  Symmetric = false
FEATURE [Part::Fillet] Fillet014  label="solenoidDriverSideBarFillet014"
  Base = -> Extrude024
  Edges = 1 edges r=1.4: [Edge14]
  Placement = pos=(0,0.9,-0.45) rot=(0,0,1;0rad)
FEATURE [Part::Revolution] Revolve  label="mainScrewStandRevolve"
  Angle = 360
  Axis = (0,0,1)
  Base = (0,0,0)
  FaceMakerClass = Part::FaceMakerBullseye
  Placement = pos=(121.35,-15.3,0) rot=(0,0,1;0rad)
  Solid = true
  Source = -> Sketch004
  Symmetric = false
FEATURE [Part::Extrusion] Extrude021  label="solenoidDriverTopLipLowerExtrude011"
  Base = -> Sketch024
  Dir = (0,0.894389,-0.447291)
  DirMode = 2
  FaceMakerClass = Part::FaceMakerBullseye
  LengthFwd = 5.05
  LengthRev = 0
  Solid = true
  Symmetric = false
FEATURE [Part::Fillet] Fillet012  label="solenoidDriverTopLipLowerFillet004"
  Base = -> Extrude021
  Edges = 1 edges r=1.2: [Edge7]
  Placement = pos=(0,-0.9,-1.35) rot=(0,0,1;0rad)
FEATURE [Part::Fillet] Fillet003  label="solenoidDriverTopLipLowerFillet003"
  Base = -> Extrude010
  Edges = 1 edges r=1.2: [Edge7]
  Placement = pos=(0,-3,-0.3) rot=(0,0,1;0rad)
FEATURE [Part::Extrusion] Extrude025  label="mainBodyUpperExtrude025"
  Base = -> Sketch001
  Dir = (0,0,1)
  DirMode = 2
  FaceMakerClass = Part::FaceMakerBullseye
  LengthFwd = 20
  LengthRev = 0
  Solid = true
  Symmetric = false
FEATURE [Part::MultiFuse] Fusion  label="solenoidDriverBottomLipFusion"
  Placement = pos=(0,-1.6,0) rot=(0,0,1;0rad)
  Shapes = -> [Fillet005,Fillet013,Extrude023,Extrude013]
FEATURE [Sketcher::SketchObject] Sketch028
  FullyConstrained = true
  Placement = pos=(0,-14.3,2.37) rot=(-1,0,0;2.03453rad)
  sketch-geometry (4):
    g0: LineSegment StartX=0 StartY=1.5 StartZ=0 EndX=0 EndY=0 EndZ=0
    g1: LineSegment StartX=0 StartY=1.5 StartZ=0 EndX=5 EndY=1.5 EndZ=0
    g2: LineSegment StartX=5 StartY=1.5 StartZ=0 EndX=5 EndY=0 EndZ=0
    g3: LineSegment StartX=0 StartY=0 StartZ=0 EndX=5 EndY=0 EndZ=0
  constraints (13):
    c: Vertical(g0)
    c: Distance(g0) = 1.5
    c: Horizontal(g1)
    c: Distance(g1) = 5
    c: Coincident(g1,g0)
    c: Vertical(g2)
    c: Distance(g2) = 1.5
    c: Coincident(g2,g1)
    c: Block(g1)
    c: Block(g2)
    c: Block(g0)
    c: Coincident(g3,g0)
    c: Coincident(g3,g2)
FEATURE [Part::Extrusion] Extrude026  label="solenoidDriverBottomLipTopExtrude016"
  Base = -> Sketch028
  Dir = (0,0.894389,-0.447291)
  DirMode = 2
  FaceMakerClass = Part::FaceMakerBullseye
  LengthFwd = -6.5
  LengthRev = 0
  Placement = pos=(5,-14.15,19.65) rot=(1,0,0;1.5708rad)
  Solid = true
  Symmetric = false
FEATURE [Sketcher::SketchObject] Sketch029
  FullyConstrained = true
  Placement = pos=(0,-14.3,2.37) rot=(-1,0,0;2.03453rad)
  sketch-geometry (4):
    g0: LineSegment StartX=0 StartY=1.5 StartZ=0 EndX=0 EndY=0 EndZ=0
    g1: LineSegment StartX=0 StartY=1.5 StartZ=0 EndX=5 EndY=1.5 EndZ=0
    g2: LineSegment StartX=5 StartY=1.5 StartZ=0 EndX=5 EndY=0 EndZ=0
    g3: LineSegment StartX=0 StartY=0 StartZ=0 EndX=5 EndY=0 EndZ=0
  constraints (13):
    c: Vertical(g0)
    c: Distance(g0) = 1.5
    c: Horizontal(g1)
    c: Distance(g1) = 5
    c: Coincident(g1,g0)
    c: Vertical(g2)
    c: Distance(g2) = 1.5
    c: Coincident(g2,g1)
    c: Block(g1)
    c: Block(g2)
    c: Block(g0)
    c: Coincident(g3,g0)
    c: Coincident(g3,g2)
FEATURE [Part::Extrusion] Extrude027  label="solenoidDriverBottomLipTopExtrude017"
  Base = -> Sketch029
  Dir = (0,0.894389,-0.447291)
  DirMode = 2
  FaceMakerClass = Part::FaceMakerBullseye
  LengthFwd = -6.5
  LengthRev = 0
  Placement = pos=(0,-14.15,19.65) rot=(1,0,0;1.5708rad)
  Solid = true
  Symmetric = false
FEATURE [Sketcher::SketchObject] Sketch030
  FullyConstrained = true
  Placement = pos=(0,-14.3,2.37) rot=(-1,0,0;2.03453rad)
  sketch-geometry (4):
    g0: LineSegment StartX=0 StartY=1.5 StartZ=0 EndX=0 EndY=0 EndZ=0
    g1: LineSegment StartX=0 StartY=1.5 StartZ=0 EndX=5 EndY=1.5 EndZ=0
    g2: LineSegment StartX=5 StartY=1.5 StartZ=0 EndX=5 EndY=0 EndZ=0
    g3: LineSegment StartX=0 StartY=0 StartZ=0 EndX=5 EndY=0 EndZ=0
  constraints (13):
    c: Vertical(g0)
    c: Distance(g0) = 1.5
    c: Horizontal(g1)
    c: Distance(g1) = 5
    c: Coincident(g1,g0)
    c: Vertical(g2)
    c: Distance(g2) = 1.5
    c: Coincident(g2,g1)
    c: Block(g1)
    c: Block(g2)
    c: Block(g0)
    c: Coincident(g3,g0)
    c: Coincident(g3,g2)
FEATURE [Sketcher::SketchObject] Sketch031
  FullyConstrained = true
  Placement = pos=(0,-14.3,2.37) rot=(-1,0,0;2.03453rad)
  sketch-geometry (6):
    g0: LineSegment StartX=45.5 StartY=-21.2 StartZ=0 EndX=49.5 EndY=-21.2 EndZ=0
    g1: LineSegment StartX=45.5 StartY=0 StartZ=0 EndX=49.5 EndY=0 EndZ=0
    g2: LineSegment StartX=49.5 StartY=0 StartZ=0 EndX=49.5 EndY=-21.2 EndZ=0
    g3: LineSegment StartX=4 StartY=0 StartZ=0 EndX=4 EndY=-21.2 EndZ=0
    g4: LineSegment StartX=45.5 StartY=-21.2 StartZ=0 EndX=4 EndY=-21.2 EndZ=0
    g5: LineSegment StartX=4 StartY=0 StartZ=0 EndX=45.5 EndY=0 EndZ=0
  constraints (16):
    c: Horizontal(g0)
    c: Distance(g0) = 4
    c: Horizontal(g1)
    c: Distance(g1) = 4
    c: Coincident(g2,g1)
    c: Coincident(g2,g0)
    c: Vertical(g2)
    c: Block(g2)
    c: Vertical(g3)
    c: Coincident(g4,g0)
    c: Horizontal(g4)
    c: Coincident(g4,g3)
    c: Coincident(g5,g1)
    c: Horizontal(g5)
    c: Block(g3)
    c: Block(g5)
FEATURE [Part::Extrusion] Extrude028  label="removeFromSolenoidDriverMainExtrude021"
  Base = -> Sketch031
  Dir = (0,0.894389,-0.447291)
  DirMode = 2
  FaceMakerClass = Part::FaceMakerBullseye
  LengthFwd = 3.1
  LengthRev = 0
  Placement = pos=(-4,-2.42,-0.8) rot=(0,0,1;0rad)
  Solid = true
  Symmetric = false
FEATURE [Part::Extrusion] Extrude029  label="solenoidDriverBottomLipTopExtrude018"
  Base = -> Sketch030
  Dir = (0,0.894389,-0.447291)
  DirMode = 2
  FaceMakerClass = Part::FaceMakerBullseye
  LengthFwd = -6.5
  LengthRev = 0
  Placement = pos=(5,-14.15,19.65) rot=(1,0,0;1.5708rad)
  Solid = true
  Symmetric = false
FEATURE [Sketcher::SketchObject] Sketch032
  FullyConstrained = true
  Placement = pos=(0,-14.3,2.37) rot=(-1,0,0;2.03453rad)
  sketch-geometry (4):
    g0: LineSegment StartX=0 StartY=1.5 StartZ=0 EndX=0 EndY=0 EndZ=0
    g1: LineSegment StartX=0 StartY=1.5 StartZ=0 EndX=5 EndY=1.5 EndZ=0
    g2: LineSegment StartX=5 StartY=1.5 StartZ=0 EndX=5 EndY=0 EndZ=0
    g3: LineSegment StartX=0 StartY=0 StartZ=0 EndX=5 EndY=0 EndZ=0
  constraints (13):
    c: Vertical(g0)
    c: Distance(g0) = 1.5
    c: Horizontal(g1)
    c: Distance(g1) = 5
    c: Coincident(g1,g0)
    c: Vertical(g2)
    c: Distance(g2) = 1.5
    c: Coincident(g2,g1)
    c: Block(g1)
    c: Block(g2)
    c: Block(g0)
    c: Coincident(g3,g0)
    c: Coincident(g3,g2)
FEATURE [Part::Extrusion] Extrude030  label="solenoidDriverBottomLipTopExtrude019"
  Base = -> Sketch032
  Dir = (0,0.894389,-0.447291)
  DirMode = 2
  FaceMakerClass = Part::FaceMakerBullseye
  LengthFwd = -6.5
  LengthRev = 0
  Placement = pos=(0,-14.15,19.65) rot=(1,0,0;1.5708rad)
  Solid = true
  Symmetric = false
FEATURE [Part::MultiFuse] Fusion004
  Placement = pos=(0,1.4,2.65) rot=(0,0,1;0rad)
  Shapes = -> [Extrude029,Extrude030]
FEATURE [Part::MultiFuse] Fusion003
  Placement = pos=(-2.3,0,0) rot=(0,0,1;0rad)
  Shapes = -> [Extrude028,Fusion004]
FEATURE [Sketcher::SketchObject] Sketch033
  FullyConstrained = true
  Placement = pos=(0,-14.3,2.37) rot=(-1,0,0;2.03453rad)
  sketch-geometry (4):
    g0: LineSegment StartX=0 StartY=1.5 StartZ=0 EndX=0 EndY=0 EndZ=0
    g1: LineSegment StartX=0 StartY=1.5 StartZ=0 EndX=5 EndY=1.5 EndZ=0
    g2: LineSegment StartX=5 StartY=1.5 StartZ=0 EndX=5 EndY=0 EndZ=0
    g3: LineSegment StartX=0 StartY=0 StartZ=0 EndX=5 EndY=0 EndZ=0
  constraints (13):
    c: Vertical(g0)
    c: Distance(g0) = 1.5
    c: Horizontal(g1)
    c: Distance(g1) = 5
    c: Coincident(g1,g0)
    c: Vertical(g2)
    c: Distance(g2) = 1.5
    c: Coincident(g2,g1)
    c: Block(g1)
    c: Block(g2)
    c: Block(g0)
    c: Coincident(g3,g0)
    c: Coincident(g3,g2)
FEATURE [Sketcher::SketchObject] Sketch034
  FullyConstrained = true
  Placement = pos=(0,-14.3,2.37) rot=(-1,0,0;2.03453rad)
  sketch-geometry (4):
    g0: LineSegment StartX=0 StartY=1.5 StartZ=0 EndX=0 EndY=0 EndZ=0
    g1: LineSegment StartX=0 StartY=1.5 StartZ=0 EndX=5 EndY=1.5 EndZ=0
    g2: LineSegment StartX=5 StartY=1.5 StartZ=0 EndX=5 EndY=0 EndZ=0
    g3: LineSegment StartX=0 StartY=0 StartZ=0 EndX=5 EndY=0 EndZ=0
  constraints (13):
    c: Vertical(g0)
    c: Distance(g0) = 1.5
    c: Horizontal(g1)
    c: Distance(g1) = 5
    c: Coincident(g1,g0)
    c: Vertical(g2)
    c: Distance(g2) = 1.5
    c: Coincident(g2,g1)
    c: Block(g1)
    c: Block(g2)
    c: Block(g0)
    c: Coincident(g3,g0)
    c: Coincident(g3,g2)
FEATURE [Part::Extrusion] Extrude020  label="removeFromSolenoidDriverMainExtrude020"
  Base = -> Sketch020
  Dir = (0,0.894389,-0.447291)
  DirMode = 2
  FaceMakerClass = Part::FaceMakerBullseye
  LengthFwd = 3.1
  LengthRev = 0
  Placement = pos=(-4,-2.42,-0.8) rot=(0,0,1;0rad)
  Solid = true
  Symmetric = false
FEATURE [Part::Fillet] Fillet
  Base = -> Fusion003
  Edges = 1 edges r=10: [Edge5]
  Placement = pos=(-2,0,0) rot=(0,0,1;0rad)
FEATURE [Part::MultiFuse] Fusion001
  Placement = pos=(0,1.4,2.65) rot=(0,0,1;0rad)
  Shapes = -> [Extrude026,Extrude027]
FEATURE [Part::MultiFuse] Fusion002
  Shapes = -> [Extrude020,Fusion001]
FEATURE [Sketcher::SketchObject] Sketch035
  FullyConstrained = true
  Placement = pos=(0,-14.3,2.37) rot=(-1,0,0;2.03453rad)
  sketch-geometry (4):
    g0: LineSegment StartX=0 StartY=1.5 StartZ=0 EndX=0 EndY=0 EndZ=0
    g1: LineSegment StartX=0 StartY=1.5 StartZ=0 EndX=5 EndY=1.5 EndZ=0
    g2: LineSegment StartX=5 StartY=1.5 StartZ=0 EndX=5 EndY=0 EndZ=0
    g3: LineSegment StartX=0 StartY=0 StartZ=0 EndX=5 EndY=0 EndZ=0
  constraints (13):
    c: Vertical(g0)
    c: Distance(g0) = 1.5
    c: Horizontal(g1)
    c: Distance(g1) = 5
    c: Coincident(g1,g0)
    c: Vertical(g2)
    c: Distance(g2) = 1.5
    c: Coincident(g2,g1)
    c: Block(g1)
    c: Block(g2)
    c: Block(g0)
    c: Coincident(g3,g0)
    c: Coincident(g3,g2)
FEATURE [Sketcher::SketchObject] Sketch036
  FullyConstrained = true
  Placement = pos=(0,-14.3,2.37) rot=(-1,0,0;2.03453rad)
  sketch-geometry (4):
    g0: LineSegment StartX=0 StartY=1.5 StartZ=0 EndX=0 EndY=0 EndZ=0
    g1: LineSegment StartX=0 StartY=1.5 StartZ=0 EndX=5 EndY=1.5 EndZ=0
    g2: LineSegment StartX=5 StartY=1.5 StartZ=0 EndX=5 EndY=0 EndZ=0
    g3: LineSegment StartX=0 StartY=0 StartZ=0 EndX=5 EndY=0 EndZ=0
  constraints (13):
    c: Vertical(g0)
    c: Distance(g0) = 1.5
    c: Horizontal(g1)
    c: Distance(g1) = 5
    c: Coincident(g1,g0)
    c: Vertical(g2)
    c: Distance(g2) = 1.5
    c: Coincident(g2,g1)
    c: Block(g1)
    c: Block(g2)
    c: Block(g0)
    c: Coincident(g3,g0)
    c: Coincident(g3,g2)
FEATURE [Part::Extrusion] Extrude031  label="solenoidDriverBottomLipTopExtrude020"
  Base = -> Sketch035
  Dir = (0,0.894389,-0.447291)
  DirMode = 2
  FaceMakerClass = Part::FaceMakerBullseye
  LengthFwd = -6.5
  LengthRev = 0
  Placement = pos=(5,-14.15,19.65) rot=(1,0,0;1.5708rad)
  Solid = true
  Symmetric = false
FEATURE [Part::Extrusion] Extrude032  label="solenoidDriverBottomLipTopExtrude021"
  Base = -> Sketch036
  Dir = (0,0.894389,-0.447291)
  DirMode = 2
  FaceMakerClass = Part::FaceMakerBullseye
  LengthFwd = -6.5
  LengthRev = 0
  Placement = pos=(0,-14.15,19.65) rot=(1,0,0;1.5708rad)
  Solid = true
  Symmetric = false
FEATURE [Part::MultiFuse] Fusion009
  Placement = pos=(8,1.4,2.65) rot=(0,0,1;0rad)
  Shapes = -> [Extrude031,Extrude032]
FEATURE [Part::MultiFuse] Fusion010  label="removeFromSolenoidDriver"
  Shapes = -> [Fusion009,Fillet,Fusion002]
FEATURE [Sketcher::SketchObject] Sketch037
  FullyConstrained = true
  Placement = pos=(0,0,0) rot=(1,0,0;1.5708rad)
  sketch-geometry (4):
    g0: Circle CenterX=64.05 CenterY=16.5 CenterZ=0 NormalX=0 NormalY=0 NormalZ=1 AngleXU=0 Radius=2.7
    g1: Circle CenterX=64.05 CenterY=8.5 CenterZ=0 NormalX=0 NormalY=0 NormalZ=1 AngleXU=0 Radius=2.7
    g2: Circle CenterX=84.15 CenterY=8.5 CenterZ=0 NormalX=0 NormalY=0 NormalZ=1 AngleXU=0 Radius=2.7
    g3: Circle CenterX=84.15 CenterY=16.5 CenterZ=0 NormalX=0 NormalY=0 NormalZ=1 AngleXU=0 Radius=2.7
  constraints (4):
    c: Block(g2)
    c: Block(g3)
    c: Block(g0)
    c: Block(g1)
FEATURE [Part::Extrusion] Extrude033  label="removeFromMainBodyToCreateScrewHoleCounterSinks001"
  Base = -> Sketch037
  Dir = (0,-1,1.1e-15)
  DirMode = 2
  FaceMakerClass = Part::FaceMakerBullseye
  LengthFwd = 1.9
  LengthRev = 0
  Placement = pos=(0.8,0,0) rot=(0,0,1;0rad)
  Solid = true
  Symmetric = false
FEATURE [Part::MultiFuse] Fusion011  label="removeFromMainBodyToCreateScrewHoleCounterSinks001Fusion011"
  Shapes = -> [Extrude014,Extrude033]
FEATURE [Sketcher::SketchObject] Sketch038
  FullyConstrained = true
  Placement = pos=(0,-14.3,2.37) rot=(-1,0,0;2.03453rad)
  sketch-geometry (4):
    g0: LineSegment StartX=33.9 StartY=-9.7 StartZ=0 EndX=33.9 EndY=-1.5 EndZ=0
    g1: LineSegment StartX=33.9 StartY=-1.5 StartZ=0 EndX=44.5 EndY=-1.5 EndZ=0
    g2: LineSegment StartX=33.9 StartY=-9.7 StartZ=0 EndX=44.5 EndY=-9.7 EndZ=0
    g3: LineSegment StartX=44.5 StartY=-1.5 StartZ=0 EndX=44.5 EndY=-9.7 EndZ=0
  constraints (10):
    c: Vertical(g0)
    c: Coincident(g1,g0)
    c: Horizontal(g1)
    c: Block(g1)
    c: Block(g0)
    c: Coincident(g2,g0)
    c: Horizontal(g2)
    c: Coincident(g3,g1)
    c: Coincident(g3,g2)
    c: Vertical(g3)
FEATURE [Part::Extrusion] Extrude034
  Base = -> Sketch038
  Dir = (0,0.894389,-0.447291)
  DirMode = 2
  FaceMakerClass = Part::FaceMakerBullseye
  LengthFwd = 16
  LengthRev = 0
  Placement = pos=(0,-22,7) rot=(0,0,1;0rad)
  Solid = true
  Symmetric = false
FEATURE [Sketcher::SketchObject] Sketch039
  FullyConstrained = true
  Placement = pos=(0,-14.3,2.37) rot=(-1,0,0;2.03453rad)
  sketch-geometry (4):
    g0: LineSegment StartX=5.5 StartY=-7.7 StartZ=0 EndX=13.3 EndY=-7.7 EndZ=0
    g1: LineSegment StartX=13.3 StartY=-7.7 StartZ=0 EndX=13.3 EndY=-13.1 EndZ=0
    g2: LineSegment StartX=13.3 StartY=-13.1 StartZ=0 EndX=5.5 EndY=-13.1 EndZ=0
    g3: LineSegment StartX=5.5 StartY=-7.7 StartZ=0 EndX=5.5 EndY=-13.1 EndZ=0
  constraints (12):
    c: Horizontal(g0)
    c: Distance(g0) = 7.8
    c: Coincident(g1,g0)
    c: Vertical(g1)
    c: Distance(g1) = 5.4
    c: Coincident(g2,g1)
    c: Horizontal(g2)
    c: Vertical(g3)
    c: Coincident(g3,g2)
    c: Block(g0)
    c: Block(g2)
    c: Block(g3)
FEATURE [Part::Extrusion] Extrude035  label="removeToMakeHoleForConnectorExtrude035"
  Base = -> Sketch039
  Dir = (0,0.894389,-0.447291)
  DirMode = 2
  FaceMakerClass = Part::FaceMakerBullseye
  LengthFwd = 15
  LengthRev = 0
  Placement = pos=(-4,-22,9.6469) rot=(0,0,1;0rad)
  Solid = true
  Symmetric = false
FEATURE [App::MeasureDistance] Distance  label="Distance: 4.00 mm"
  Distance = 4.00184
  P1 = (119.349,-15.3,8)
  P2 = (123.351,-15.3,8)
FEATURE [App::MeasureDistance] Distance001  label="Distance: 3.80 mm"
  Distance = 3.8
  P1 = (119.45,-15.3,8)
  P2 = (123.25,-15.3,8)
FEATURE [Part::Fillet] Fillet015
  Base = -> Extrude009
  Edges = 1 edges r=1.59: [Edge7]
FEATURE [Part::Fillet] Fillet016
  Base = -> Extrude017
  Edges = 1 edges r=1.49: [Edge12]
FEATURE [Part::Fillet] Fillet017
  Base = -> Fillet016
  Edges = 1 edges r=1.45: [Edge8]
FEATURE [Part::MultiFuse] Fusion012  label="main"
  Shapes = -> [Extrude,Revolve,Extrude005,Fillet003,Fillet012,Fillet014,Extrude025,Fusion,Fillet015,Fillet017]
FEATURE [Part::Cut] Cut001
  Base = -> Fusion012
  Tool = -> Box003
FEATURE [Part::Cut] Cut002
  Base = -> Cut001
  Tool = -> Box002
FEATURE [Part::Cut] Cut003
  Base = -> Cut002
  Tool = -> Cut
FEATURE [Part::Cut] Cut004
  Base = -> Cut003
  Tool = -> Extrude019
FEATURE [Part::Cut] Cut005
  Base = -> Cut004
  Tool = -> Fusion011
FEATURE [Part::Cut] Cut006
  Base = -> Cut005
  Tool = -> Extrude004
FEATURE [Part::Cut] Cut007
  Base = -> Cut006
  Tool = -> Extrude015
FEATURE [Part::Cut] Cut008
  Base = -> Cut007
  Tool = -> Extrude008
FEATURE [Part::Cut] Cut009
  Base = -> Cut008
  Tool = -> Fusion010
FEATURE [App::MeasureDistance] Distance002  label="Distance: 2.05 mm"
  Distance = 2.05453
  P1 = (1.5,-23.0732,21.402)
  P2 = (6e-15,-23,20)
FEATURE [Part::Cut] Cut010
  Base = -> Cut009
  Tool = -> Extrude035
FEATURE [Part::Cut] Cut011
  Base = -> Cut010
  Tool = -> Extrude034
FEATURE [Part::Box] Box004  label="Cube004"
  AttacherType = Attacher::AttachEngine3D
  Height = 10
  Length = 200
  Placement = pos=(-30,0,0) rot=(0,0,1;0rad)
  Width = 10
FEATURE [Part::Fillet] Fillet020
  Base = -> Box004
  Edges = 1 edges r=3.6: [Edge12]
FEATURE [Part::Box] Box005  label="Cube005"
  AttacherType = Attacher::AttachEngine3D
  Height = 10
  Length = 198
  Placement = pos=(-30,0,0) rot=(0,0,1;0rad)
  Width = 10
FEATURE [Part::Cut] Cut012
  Base = -> Box005
  Tool = -> Fillet020
FEATURE [Part::Box] Box006  label="Cube006"
  AttacherType = Attacher::AttachEngine3D
  Height = 5
  Length = 200
  Placement = pos=(-30,6.4,10) rot=(1,0,0;0rad)
  Width = 5
FEATURE [Part::Box] Box007  label="Cube007"
  AttacherType = Attacher::AttachEngine3D
  Height = 5
  Length = 200
  Placement = pos=(-30,6.4,10) rot=(1,0,0;0.872665rad)
  Width = 5
FEATURE [Part::MultiFuse] Fusion013  label="removeFromMainFusion013"
  Placement = pos=(0,-10,10) rot=(0,0,1;0rad)
  Shapes = -> [Box007,Box006,Cut012]
FEATURE [Mesh::Feature] v0_98_Cut013  label="v0_98-Cut013"
FEATURE [App::MeasureDistance] Distance003  label="Distance: 7.18 mm"
  Distance = 7.17719
  P1 = (117.773,-15.3145,-2.4)
  P2 = (124.951,-15.2973,-2.4)
FEATURE [Sketcher::SketchObject] Sketch040
  FullyConstrained = true
  Placement = pos=(0,-14.3,2.37) rot=(-1,0,0;2.03453rad)
  sketch-geometry (4):
    g0: LineSegment StartX=0 StartY=1.5 StartZ=0 EndX=0 EndY=0 EndZ=0
    g1: LineSegment StartX=0 StartY=1.5 StartZ=0 EndX=5 EndY=1.5 EndZ=0
    g2: LineSegment StartX=5 StartY=1.5 StartZ=0 EndX=5 EndY=0 EndZ=0
    g3: LineSegment StartX=0 StartY=0 StartZ=0 EndX=5 EndY=0 EndZ=0
  constraints (13):
    c: Vertical(g0)
    c: Distance(g0) = 1.5
    c: Horizontal(g1)
    c: Distance(g1) = 5
    c: Coincident(g1,g0)
    c: Vertical(g2)
    c: Distance(g2) = 1.5
    c: Coincident(g2,g1)
    c: Block(g1)
    c: Block(g2)
    c: Block(g0)
    c: Coincident(g3,g0)
    c: Coincident(g3,g2)
FEATURE [Part::Extrusion] Extrude036
  Base = -> Sketch040
  Dir = (0,0.894389,-0.447291)
  DirMode = 2
  FaceMakerClass = Part::FaceMakerBullseye
  LengthFwd = 1.4
  LengthRev = 0
  Placement = pos=(0,8.25,17.58) rot=(0,0,1;0rad)
  Solid = true
  Symmetric = false
FEATURE [Sketcher::SketchObject] Sketch041
  FullyConstrained = true
  Placement = pos=(0,-14.3,2.37) rot=(-1,0,0;2.03453rad)
  sketch-geometry (4):
    g0: LineSegment StartX=0 StartY=1.5 StartZ=0 EndX=0 EndY=0 EndZ=0
    g1: LineSegment StartX=0 StartY=1.5 StartZ=0 EndX=5 EndY=1.5 EndZ=0
    g2: LineSegment StartX=5 StartY=1.5 StartZ=0 EndX=5 EndY=0 EndZ=0
    g3: LineSegment StartX=0 StartY=0 StartZ=0 EndX=5 EndY=0 EndZ=0
  constraints (13):
    c: Vertical(g0)
    c: Distance(g0) = 1.5
    c: Horizontal(g1)
    c: Distance(g1) = 5
    c: Coincident(g1,g0)
    c: Vertical(g2)
    c: Distance(g2) = 1.5
    c: Coincident(g2,g1)
    c: Block(g1)
    c: Block(g2)
    c: Block(g0)
    c: Coincident(g3,g0)
    c: Coincident(g3,g2)
FEATURE [Part::Extrusion] Extrude037
  Base = -> Sketch041
  Dir = (0,0.894389,-0.447291)
  DirMode = 2
  FaceMakerClass = Part::FaceMakerBullseye
  LengthFwd = 1.4
  LengthRev = 0
  Placement = pos=(0,6.11,13.33) rot=(0,0,1;0rad)
  Solid = true
  Symmetric = false
FEATURE [Part::MultiFuse] Fusion014  label="screwSpacerFusion014"
  Shapes = -> [Extrude037,Extrude036]
FEATURE [Sketcher::SketchObject] Sketch042
  FullyConstrained = true
  Placement = pos=(0,-14.3,2.37) rot=(-1,0,0;2.03453rad)
  sketch-geometry (4):
    g0: LineSegment StartX=0 StartY=1.5 StartZ=0 EndX=0 EndY=0 EndZ=0
    g1: LineSegment StartX=0 StartY=1.5 StartZ=0 EndX=5 EndY=1.5 EndZ=0
    g2: LineSegment StartX=5 StartY=1.5 StartZ=0 EndX=5 EndY=0 EndZ=0
    g3: LineSegment StartX=0 StartY=0 StartZ=0 EndX=5 EndY=0 EndZ=0
  constraints (13):
    c: Vertical(g0)
    c: Distance(g0) = 1.5
    c: Horizontal(g1)
    c: Distance(g1) = 5
    c: Coincident(g1,g0)
    c: Vertical(g2)
    c: Distance(g2) = 1.5
    c: Coincident(g2,g1)
    c: Block(g1)
    c: Block(g2)
    c: Block(g0)
    c: Coincident(g3,g0)
    c: Coincident(g3,g2)
FEATURE [Part::Extrusion] Extrude038
  Base = -> Sketch042
  Dir = (0,0.894389,-0.447291)
  DirMode = 2
  FaceMakerClass = Part::FaceMakerBullseye
  LengthFwd = 1.4
  LengthRev = 0
  Placement = pos=(0,8.459,18) rot=(0,0,1;0rad)
  Solid = true
  Symmetric = false
FEATURE [Part::MultiFuse] Fusion015  label="screwSpacerFusion014Fusion015"
  Placement = pos=(0,0.35,-0.18) rot=(0,0,1;0rad)
  Shapes = -> [Extrude038,Fusion014]
FEATURE [Part::Cylinder] Cylinder
  Angle = 360
  AttacherType = Attacher::AttachEngine3D
  Height = 10
  Placement = pos=(0,10,0) rot=(0,0,1;0rad)
  Radius = 1.5
FEATURE [Part::Cylinder] Cylinder001
  Angle = 360
  AttacherType = Attacher::AttachEngine3D
  Height = 10
  Placement = pos=(3,10,0) rot=(0,0,1;0rad)
  Radius = 1.5
FEATURE [Part::Box] Box008  label="Cube008"
  AttacherType = Attacher::AttachEngine3D
  Height = 10
  Length = 3
  Placement = pos=(0,8.5,0) rot=(0,0,1;0rad)
  Width = 3
FEATURE [Part::MultiFuse] Fusion016  label="holeForWireFusion016"
  Shapes = -> [Cylinder001,Box008,Cylinder]
FEATURE [Part::Box] Box009  label="Cube009"
  AttacherType = Attacher::AttachEngine3D
  Height = 10
  Length = 3
  Placement = pos=(0,8.5,0) rot=(0,0,1;0rad)
  Width = 3
FEATURE [Part::Cylinder] Cylinder002
  Angle = 360
  AttacherType = Attacher::AttachEngine3D
  Height = 10
  Placement = pos=(0,10,0) rot=(0,0,1;0rad)
  Radius = 1.5
FEATURE [Part::Cylinder] Cylinder003
  Angle = 360
  AttacherType = Attacher::AttachEngine3D
  Height = 10
  Placement = pos=(3,10,0) rot=(0,0,1;0rad)
  Radius = 1.5
FEATURE [Part::MultiFuse] Fusion017  label="holeForWireFusion017"
  Placement = pos=(0,0,10) rot=(0,0,1;0rad)
  Shapes = -> [Cylinder003,Box009,Cylinder002]
FEATURE [Part::MultiFuse] Fusion018  label="holeForWireFusion018"
  Placement = pos=(0,0,0) rot=(0,1,0;-1.5708rad)
  Shapes = -> [Fusion017,Fusion016]
FEATURE [Part::Box] Box010  label="Cube010"
  AttacherType = Attacher::AttachEngine3D
  Height = 0.1
  Length = 0.1
  Placement = pos=(-2,10,0) rot=(0,0.995037,0.099504;0rad)
  Width = 0.1
FEATURE [Part::MultiFuse] Fusion019
  Placement = pos=(0,10,0) rot=(1,0,0;1.5708rad)
  Shapes = -> [Box010,Fusion018]
FEATURE [Part::Box] Box011  label="Cube011"
  AttacherType = Attacher::AttachEngine3D
  Height = 0.1
  Length = 1.1
  Placement = pos=(-2,10,10) rot=(0,0.995037,0.099504;0rad)
  Width = 0.1
FEATURE [Part::MultiFuse] Fusion020
  Placement = pos=(0,0,0) rot=(0,1,0;0.349066rad)
  Shapes = -> [Box011,Fusion019]
FEATURE [Part::Box] Box012  label="Cube012"
  AttacherType = Attacher::AttachEngine3D
  Height = 0.1
  Length = 1.1
  Placement = pos=(-2,10,10) rot=(0,0.995037,0.099504;0rad)
  Width = 0.1
FEATURE [Part::MultiFuse] Fusion021
  Placement = pos=(0,30,0) rot=(0,0,1;-2.6529rad)
  Shapes = -> [Box012,Fusion020]
FEATURE [Part::Box] Box013  label="Cube013"
  AttacherType = Attacher::AttachEngine3D
  Height = 0.1
  Length = 1.1
  Placement = pos=(2,19,10) rot=(0,0.995037,0.099504;0rad)
  Width = 0.1
FEATURE [Part::MultiFuse] Fusion022  label="holeForWire"
  Placement = pos=(15,-49.8,-8.2) rot=(0,0,1;0rad)
  Shapes = -> [Box013,Fusion021]
FEATURE [Part::Cut] Cut013
  Base = -> Cut011
  Tool = -> Fusion013
FEATURE [Part::Cut] Cut014
  Base = -> Cut013
  Tool = -> Fusion022
FEATURE [Sketcher::SketchObject] Sketch043
  FullyConstrained = true
  MapMode = 4
  Placement = pos=(0,0,0) rot=(0.57735,0.57735,0.57735;2.0944rad)
  Support = -> [Cut014]
  sketch-geometry (14):
    g0: LineSegment StartX=6.08745 StartY=-4.11588 StartZ=0 EndX=6.08745 EndY=-2.11589 EndZ=0
    g1: LineSegment StartX=3.58745 StartY=2.38411 StartZ=0 EndX=3.58745 EndY=4.38411 EndZ=0
    g2: LineSegment StartX=8.08745 StartY=1.38411 StartZ=0 EndX=8.08745 EndY=-1.11589 EndZ=0
    g3: ArcOfCircle CenterX=7.08745 CenterY=-1.11589 CenterZ=0 NormalX=0 NormalY=0 NormalZ=1 AngleXU=0 Radius=1 StartAngle=4.71239 EndAngle=6.28319
    g4: LineSegment StartX=6.08745 StartY=-2.11589 StartZ=0 EndX=7.08745 EndY=-2.11589 EndZ=0
    g5: LineSegment StartX=6.08745 StartY=-4.11588 StartZ=0 EndX=7.08745 EndY=-4.11588 EndZ=0
    g6: ArcOfCircle CenterX=7.08745 CenterY=-1.11589 CenterZ=0 NormalX=0 NormalY=0 NormalZ=1 AngleXU=0 Radius=3 StartAngle=4.71239 EndAngle=6.28319
    g7: ArcOfCircle CenterX=7.08745 CenterY=1.38411 CenterZ=0 NormalX=0 NormalY=0 NormalZ=1 AngleXU=0 Radius=1 StartAngle=5.35e-14 EndAngle=1.5708
    g8: LineSegment StartX=3.58745 StartY=4.38411 StartZ=0 EndX=7.08745 EndY=4.38411 EndZ=0
    g9: LineSegment StartX=10.0875 StartY=-1.11588 StartZ=0 EndX=10.0875 EndY=1.38411 EndZ=0
    g10: ArcOfCircle CenterX=7.08745 CenterY=1.38411 CenterZ=0 NormalX=0 NormalY=0 NormalZ=1 AngleXU=0 Radius=3 StartAngle=3.57e-14 EndAngle=1.5708
    g11: LineSegment StartX=3.58745 StartY=2.38411 StartZ=0 EndX=3.58745 EndY=1.38411 EndZ=0
    g12: ArcOfCircle CenterX=4.58745 CenterY=1.38412 CenterZ=0 NormalX=0 NormalY=0 NormalZ=1 AngleXU=0 Radius=1 StartAngle=1.57081 EndAngle=3.14159
    g13: LineSegment StartX=4.58744 StartY=2.38411 StartZ=0 EndX=7.08745 EndY=2.38411 EndZ=0
  constraints (33):
    c: Vertical(g0)
    c: Vertical(g1)
    c: Distance(g1) = 2
    c: Block(g0)
    c: Block(g2)
    c: Coincident(g3,g2)
    c: Coincident(g4,g0)
    c: Coincident(g4,g3)
    c: Horizontal(g4)
    c: Block(g3)
    c: Coincident(g5,g0)
    c: Horizontal(g5)
    c: Coincident(g6,g3)
    c: Block(g6)
    c: Block(g5)
    c: Coincident(g7,g2)
    c: Block(g7)
    c: Coincident(g8,g1)
    c: Coincident(g9,g6)
    c: Vertical(g9)
    c: Coincident(g10,g7)
    c: Block(g10)
    c: Block(g8)
    c: Block(g9)
    c: Coincident(g11,g1)
    c: Vertical(g11)
    c: Distance(g11) = 1
    c: Coincident(g12,g11)
    c: Coincident(g13,g12)
    c: Coincident(g13,g7)
    c: Horizontal(g13)
    c: Block(g13)
    c: Block(g12)
FEATURE [Sketcher::SketchObject] Sketch044
  FullyConstrained = true
  MapMode = 4
  Placement = pos=(0,0,0) rot=(0.57735,0.57735,0.57735;2.0944rad)
  Support = -> [Cut014]
  sketch-geometry (14):
    g0: LineSegment StartX=6.08745 StartY=-4.11588 StartZ=0 EndX=6.08745 EndY=-2.11589 EndZ=0
    g1: LineSegment StartX=8.08745 StartY=1.38411 StartZ=0 EndX=8.08745 EndY=-1.11589 EndZ=0
    g2: ArcOfCircle CenterX=7.08745 CenterY=-1.11589 CenterZ=0 NormalX=0 NormalY=0 NormalZ=1 AngleXU=0 Radius=1 StartAngle=4.71239 EndAngle=6.28319
    g3: LineSegment StartX=6.08745 StartY=-2.11589 StartZ=0 EndX=7.08745 EndY=-2.11589 EndZ=0
    g4: LineSegment StartX=6.08745 StartY=-4.11588 StartZ=0 EndX=7.08745 EndY=-4.11588 EndZ=0
    g5: ArcOfCircle CenterX=7.08745 CenterY=-1.11589 CenterZ=0 NormalX=0 NormalY=0 NormalZ=1 AngleXU=0 Radius=3 StartAngle=4.71239 EndAngle=6.28319
    g6: ArcOfCircle CenterX=7.08745 CenterY=1.38411 CenterZ=0 NormalX=0 NormalY=0 NormalZ=1 AngleXU=0 Radius=1 StartAngle=5.35e-14 EndAngle=1.5708
    g7: LineSegment StartX=10.0875 StartY=-1.11588 StartZ=0 EndX=10.0875 EndY=1.38411 EndZ=0
    g8: ArcOfCircle CenterX=7.08745 CenterY=1.38411 CenterZ=0 NormalX=0 NormalY=0 NormalZ=1 AngleXU=0 Radius=3 StartAngle=3.57e-14 EndAngle=1.5708
    g9: ArcOfCircle CenterX=4.58745 CenterY=1.38412 CenterZ=0 NormalX=0 NormalY=0 NormalZ=1 AngleXU=0 Radius=1 StartAngle=1.57081 EndAngle=3.14159
    g10: LineSegment StartX=4.58744 StartY=2.38411 StartZ=0 EndX=7.08745 EndY=2.38411 EndZ=0
    g11: LineSegment StartX=4.58745 StartY=4.38411 StartZ=0 EndX=7.08745 EndY=4.38411 EndZ=0
    g12: ArcOfCircle CenterX=4.58745 CenterY=5.38411 CenterZ=0 NormalX=0 NormalY=0 NormalZ=1 AngleXU=0 Radius=1 StartAngle=3.14159 EndAngle=4.71239
    g13: LineSegment StartX=3.58745 StartY=5.38411 StartZ=0 EndX=3.58745 EndY=1.38411 EndZ=0
  constraints (33):
    c: Vertical(g0)
    c: Block(g0)
    c: Block(g1)
    c: Coincident(g2,g1)
    c: Coincident(g3,g0)
    c: Coincident(g3,g2)
    c: Horizontal(g3)
    c: Block(g2)
    c: Coincident(g4,g0)
    c: Horizontal(g4)
    c: Coincident(g5,g2)
    c: Block(g5)
    c: Block(g4)
    c: Coincident(g6,g1)
    c: Block(g6)
    c: Coincident(g7,g5)
    c: Vertical(g7)
    c: Coincident(g8,g6)
    c: Block(g8)
    c: Block(g7)
    c: Coincident(g10,g9)
    c: Coincident(g10,g6)
    c: Horizontal(g10)
    c: Block(g10)
    c: Block(g9)
    c: Coincident(g11,g8)
    c: Horizontal(g11)
    c: Block(g12)
    c: Block(g11)
    c: Coincident(g13,g12)
    c: Coincident(g13,g9)
    c: Vertical(g13)
    c: Tangent(g13,g9)
FEATURE [Part::Extrusion] Extrude039
  Base = -> Sketch044
  Dir = (1,0,0)
  DirMode = 2
  FaceMakerClass = Part::FaceMakerBullseye
  LengthFwd = 10
  LengthRev = 0
  Placement = pos=(8,-22.615,4.115) rot=(0,0,1;3.14159rad)
  Solid = true
  Symmetric = false
FEATURE [App::MeasureDistance] Distance004  label="Distance: 42.16 mm"
  Distance = 42.1607
  P1 = (14.6786,-26.2,1.24491)
  P2 = (-27.4815,-26.2,1.03853)
FEATURE [Sketcher::SketchObject] Sketch045
  FullyConstrained = true
  MapMode = 4
  Placement = pos=(0,0,0) rot=(0.57735,0.57735,0.57735;2.0944rad)
  Support = -> [Cut014]
  sketch-geometry (14):
    g0: LineSegment StartX=6.08745 StartY=-4.11588 StartZ=0 EndX=6.08745 EndY=-2.11589 EndZ=0
    g1: LineSegment StartX=8.08745 StartY=1.38411 StartZ=0 EndX=8.08745 EndY=-1.11589 EndZ=0
    g2: ArcOfCircle CenterX=7.08745 CenterY=-1.11589 CenterZ=0 NormalX=0 NormalY=0 NormalZ=1 AngleXU=0 Radius=1 StartAngle=4.71239 EndAngle=6.28319
    g3: LineSegment StartX=6.08745 StartY=-2.11589 StartZ=0 EndX=7.08745 EndY=-2.11589 EndZ=0
    g4: LineSegment StartX=6.08745 StartY=-4.11588 StartZ=0 EndX=7.08745 EndY=-4.11588 EndZ=0
    g5: ArcOfCircle CenterX=7.08745 CenterY=-1.11589 CenterZ=0 NormalX=0 NormalY=0 NormalZ=1 AngleXU=0 Radius=3 StartAngle=4.71239 EndAngle=6.28319
    g6: ArcOfCircle CenterX=7.08745 CenterY=1.38411 CenterZ=0 NormalX=0 NormalY=0 NormalZ=1 AngleXU=0 Radius=1 StartAngle=5.35e-14 EndAngle=1.5708
    g7: LineSegment StartX=10.0875 StartY=-1.11588 StartZ=0 EndX=10.0875 EndY=1.38411 EndZ=0
    g8: ArcOfCircle CenterX=7.08745 CenterY=1.38411 CenterZ=0 NormalX=0 NormalY=0 NormalZ=1 AngleXU=0 Radius=3 StartAngle=3.57e-14 EndAngle=1.5708
    g9: ArcOfCircle CenterX=4.58745 CenterY=1.38412 CenterZ=0 NormalX=0 NormalY=0 NormalZ=1 AngleXU=0 Radius=1 StartAngle=1.57081 EndAngle=3.14159
    g10: LineSegment StartX=4.58744 StartY=2.38411 StartZ=0 EndX=7.08745 EndY=2.38411 EndZ=0
    g11: LineSegment StartX=4.58745 StartY=4.38411 StartZ=0 EndX=7.08745 EndY=4.38411 EndZ=0
    g12: ArcOfCircle CenterX=4.58745 CenterY=5.38411 CenterZ=0 NormalX=0 NormalY=0 NormalZ=1 AngleXU=0 Radius=1 StartAngle=3.14159 EndAngle=4.71239
    g13: LineSegment StartX=3.58745 StartY=5.38411 StartZ=0 EndX=3.58745 EndY=1.38411 EndZ=0
  constraints (33):
    c: Vertical(g0)
    c: Block(g0)
    c: Block(g1)
    c: Coincident(g2,g1)
    c: Coincident(g3,g0)
    c: Coincident(g3,g2)
    c: Horizontal(g3)
    c: Block(g2)
    c: Coincident(g4,g0)
    c: Horizontal(g4)
    c: Coincident(g5,g2)
    c: Block(g5)
    c: Block(g4)
    c: Coincident(g6,g1)
    c: Block(g6)
    c: Coincident(g7,g5)
    c: Vertical(g7)
    c: Coincident(g8,g6)
    c: Block(g8)
    c: Block(g7)
    c: Coincident(g10,g9)
    c: Coincident(g10,g6)
    c: Horizontal(g10)
    c: Block(g10)
    c: Block(g9)
    c: Coincident(g11,g8)
    c: Horizontal(g11)
    c: Block(g12)
    c: Block(g11)
    c: Coincident(g13,g12)
    c: Coincident(g13,g9)
    c: Vertical(g13)
    c: Tangent(g13,g9)
FEATURE [Part::Extrusion] Extrude040
  Base = -> Sketch045
  Dir = (1,0,0)
  DirMode = 2
  FaceMakerClass = Part::FaceMakerBullseye
  LengthFwd = 10
  LengthRev = 0
  Placement = pos=(-17.5,-22.615,4.115) rot=(0,0,1;3.14159rad)
  Solid = true
  Symmetric = false
FEATURE [Sketcher::SketchObject] Sketch046
  FullyConstrained = true
  MapMode = 4
  Placement = pos=(0,0,0) rot=(0.57735,0.57735,0.57735;2.0944rad)
  Support = -> [Cut014]
  sketch-geometry (14):
    g0: LineSegment StartX=6.08745 StartY=-4.11588 StartZ=0 EndX=6.08745 EndY=-2.11589 EndZ=0
    g1: LineSegment StartX=8.08745 StartY=1.38411 StartZ=0 EndX=8.08745 EndY=-1.11589 EndZ=0
    g2: ArcOfCircle CenterX=7.08745 CenterY=-1.11589 CenterZ=0 NormalX=0 NormalY=0 NormalZ=1 AngleXU=0 Radius=1 StartAngle=4.71239 EndAngle=6.28319
    g3: LineSegment StartX=6.08745 StartY=-2.11589 StartZ=0 EndX=7.08745 EndY=-2.11589 EndZ=0
    g4: LineSegment StartX=6.08745 StartY=-4.11588 StartZ=0 EndX=7.08745 EndY=-4.11588 EndZ=0
    g5: ArcOfCircle CenterX=7.08745 CenterY=-1.11589 CenterZ=0 NormalX=0 NormalY=0 NormalZ=1 AngleXU=0 Radius=3 StartAngle=4.71239 EndAngle=6.28319
    g6: ArcOfCircle CenterX=7.08745 CenterY=1.38411 CenterZ=0 NormalX=0 NormalY=0 NormalZ=1 AngleXU=0 Radius=1 StartAngle=5.35e-14 EndAngle=1.5708
    g7: LineSegment StartX=10.0875 StartY=-1.11588 StartZ=0 EndX=10.0875 EndY=1.38411 EndZ=0
    g8: ArcOfCircle CenterX=7.08745 CenterY=1.38411 CenterZ=0 NormalX=0 NormalY=0 NormalZ=1 AngleXU=0 Radius=3 StartAngle=3.57e-14 EndAngle=1.5708
    g9: ArcOfCircle CenterX=4.58745 CenterY=1.38412 CenterZ=0 NormalX=0 NormalY=0 NormalZ=1 AngleXU=0 Radius=1 StartAngle=1.57081 EndAngle=3.14159
    g10: LineSegment StartX=4.58744 StartY=2.38411 StartZ=0 EndX=7.08745 EndY=2.38411 EndZ=0
    g11: LineSegment StartX=4.58745 StartY=4.38411 StartZ=0 EndX=7.08745 EndY=4.38411 EndZ=0
    g12: ArcOfCircle CenterX=4.58745 CenterY=5.38411 CenterZ=0 NormalX=0 NormalY=0 NormalZ=1 AngleXU=0 Radius=1 StartAngle=3.14159 EndAngle=4.71239
    g13: LineSegment StartX=3.58745 StartY=5.38411 StartZ=0 EndX=3.58745 EndY=1.38411 EndZ=0
  constraints (33):
    c: Vertical(g0)
    c: Block(g0)
    c: Block(g1)
    c: Coincident(g2,g1)
    c: Coincident(g3,g0)
    c: Coincident(g3,g2)
    c: Horizontal(g3)
    c: Block(g2)
    c: Coincident(g4,g0)
    c: Horizontal(g4)
    c: Coincident(g5,g2)
    c: Block(g5)
    c: Block(g4)
    c: Coincident(g6,g1)
    c: Block(g6)
    c: Coincident(g7,g5)
    c: Vertical(g7)
    c: Coincident(g8,g6)
    c: Block(g8)
    c: Block(g7)
    c: Coincident(g10,g9)
    c: Coincident(g10,g6)
    c: Horizontal(g10)
    c: Block(g10)
    c: Block(g9)
    c: Coincident(g11,g8)
    c: Horizontal(g11)
    c: Block(g12)
    c: Block(g11)
    c: Coincident(g13,g12)
    c: Coincident(g13,g9)
    c: Vertical(g13)
    c: Tangent(g13,g9)
FEATURE [Sketcher::SketchObject] Sketch047
  FullyConstrained = true
  MapMode = 4
  Placement = pos=(0,0,0) rot=(0.57735,0.57735,0.57735;2.0944rad)
  Support = -> [Cut014]
  sketch-geometry (14):
    g0: LineSegment StartX=6.08745 StartY=-4.11588 StartZ=0 EndX=6.08745 EndY=-2.11589 EndZ=0
    g1: LineSegment StartX=8.08745 StartY=1.38411 StartZ=0 EndX=8.08745 EndY=-1.11589 EndZ=0
    g2: ArcOfCircle CenterX=7.08745 CenterY=-1.11589 CenterZ=0 NormalX=0 NormalY=0 NormalZ=1 AngleXU=0 Radius=1 StartAngle=4.71239 EndAngle=6.28319
    g3: LineSegment StartX=6.08745 StartY=-2.11589 StartZ=0 EndX=7.08745 EndY=-2.11589 EndZ=0
    g4: LineSegment StartX=6.08745 StartY=-4.11588 StartZ=0 EndX=7.08745 EndY=-4.11588 EndZ=0
    g5: ArcOfCircle CenterX=7.08745 CenterY=-1.11589 CenterZ=0 NormalX=0 NormalY=0 NormalZ=1 AngleXU=0 Radius=3 StartAngle=4.71239 EndAngle=6.28319
    g6: ArcOfCircle CenterX=7.08745 CenterY=1.38411 CenterZ=0 NormalX=0 NormalY=0 NormalZ=1 AngleXU=0 Radius=1 StartAngle=5.35e-14 EndAngle=1.5708
    g7: LineSegment StartX=10.0875 StartY=-1.11588 StartZ=0 EndX=10.0875 EndY=1.38411 EndZ=0
    g8: ArcOfCircle CenterX=7.08745 CenterY=1.38411 CenterZ=0 NormalX=0 NormalY=0 NormalZ=1 AngleXU=0 Radius=3 StartAngle=3.57e-14 EndAngle=1.5708
    g9: ArcOfCircle CenterX=4.58745 CenterY=1.38412 CenterZ=0 NormalX=0 NormalY=0 NormalZ=1 AngleXU=0 Radius=1 StartAngle=1.57081 EndAngle=3.14159
    g10: LineSegment StartX=4.58744 StartY=2.38411 StartZ=0 EndX=7.08745 EndY=2.38411 EndZ=0
    g11: LineSegment StartX=4.58745 StartY=4.38411 StartZ=0 EndX=7.08745 EndY=4.38411 EndZ=0
    g12: ArcOfCircle CenterX=4.58745 CenterY=5.38411 CenterZ=0 NormalX=0 NormalY=0 NormalZ=1 AngleXU=0 Radius=1 StartAngle=3.14159 EndAngle=4.71239
    g13: LineSegment StartX=3.58745 StartY=5.38411 StartZ=0 EndX=3.58745 EndY=1.38411 EndZ=0
  constraints (33):
    c: Vertical(g0)
    c: Block(g0)
    c: Block(g1)
    c: Coincident(g2,g1)
    c: Coincident(g3,g0)
    c: Coincident(g3,g2)
    c: Horizontal(g3)
    c: Block(g2)
    c: Coincident(g4,g0)
    c: Horizontal(g4)
    c: Coincident(g5,g2)
    c: Block(g5)
    c: Block(g4)
    c: Coincident(g6,g1)
    c: Block(g6)
    c: Coincident(g7,g5)
    c: Vertical(g7)
    c: Coincident(g8,g6)
    c: Block(g8)
    c: Block(g7)
    c: Coincident(g10,g9)
    c: Coincident(g10,g6)
    c: Horizontal(g10)
    c: Block(g10)
    c: Block(g9)
    c: Coincident(g11,g8)
    c: Horizontal(g11)
    c: Block(g12)
    c: Block(g11)
    c: Coincident(g13,g12)
    c: Coincident(g13,g9)
    c: Vertical(g13)
    c: Tangent(g13,g9)
FEATURE [Sketcher::SketchObject] Sketch048
  FullyConstrained = true
  MapMode = 4
  Placement = pos=(0,0,0) rot=(0.57735,0.57735,0.57735;2.0944rad)
  Support = -> [Cut014]
  sketch-geometry (14):
    g0: LineSegment StartX=6.08745 StartY=-4.11588 StartZ=0 EndX=6.08745 EndY=-2.11589 EndZ=0
    g1: LineSegment StartX=8.08745 StartY=1.38411 StartZ=0 EndX=8.08745 EndY=-1.11589 EndZ=0
    g2: ArcOfCircle CenterX=7.08745 CenterY=-1.11589 CenterZ=0 NormalX=0 NormalY=0 NormalZ=1 AngleXU=0 Radius=1 StartAngle=4.71239 EndAngle=6.28319
    g3: LineSegment StartX=6.08745 StartY=-2.11589 StartZ=0 EndX=7.08745 EndY=-2.11589 EndZ=0
    g4: LineSegment StartX=6.08745 StartY=-4.11588 StartZ=0 EndX=7.08745 EndY=-4.11588 EndZ=0
    g5: ArcOfCircle CenterX=7.08745 CenterY=-1.11589 CenterZ=0 NormalX=0 NormalY=0 NormalZ=1 AngleXU=0 Radius=3 StartAngle=4.71239 EndAngle=6.28319
    g6: ArcOfCircle CenterX=7.08745 CenterY=1.38411 CenterZ=0 NormalX=0 NormalY=0 NormalZ=1 AngleXU=0 Radius=1 StartAngle=5.35e-14 EndAngle=1.5708
    g7: LineSegment StartX=10.0875 StartY=-1.11588 StartZ=0 EndX=10.0875 EndY=1.38411 EndZ=0
    g8: ArcOfCircle CenterX=7.08745 CenterY=1.38411 CenterZ=0 NormalX=0 NormalY=0 NormalZ=1 AngleXU=0 Radius=3 StartAngle=3.57e-14 EndAngle=1.5708
    g9: ArcOfCircle CenterX=4.58745 CenterY=1.38412 CenterZ=0 NormalX=0 NormalY=0 NormalZ=1 AngleXU=0 Radius=1 StartAngle=1.57081 EndAngle=3.14159
    g10: LineSegment StartX=4.58744 StartY=2.38411 StartZ=0 EndX=7.08745 EndY=2.38411 EndZ=0
    g11: LineSegment StartX=4.58745 StartY=4.38411 StartZ=0 EndX=7.08745 EndY=4.38411 EndZ=0
    g12: ArcOfCircle CenterX=4.58745 CenterY=5.38411 CenterZ=0 NormalX=0 NormalY=0 NormalZ=1 AngleXU=0 Radius=1 StartAngle=3.14159 EndAngle=4.71239
    g13: LineSegment StartX=3.58745 StartY=5.38411 StartZ=0 EndX=3.58745 EndY=1.38411 EndZ=0
  constraints (33):
    c: Vertical(g0)
    c: Block(g0)
    c: Block(g1)
    c: Coincident(g2,g1)
    c: Coincident(g3,g0)
    c: Coincident(g3,g2)
    c: Horizontal(g3)
    c: Block(g2)
    c: Coincident(g4,g0)
    c: Horizontal(g4)
    c: Coincident(g5,g2)
    c: Block(g5)
    c: Block(g4)
    c: Coincident(g6,g1)
    c: Block(g6)
    c: Coincident(g7,g5)
    c: Vertical(g7)
    c: Coincident(g8,g6)
    c: Block(g8)
    c: Block(g7)
    c: Coincident(g10,g9)
    c: Coincident(g10,g6)
    c: Horizontal(g10)
    c: Block(g10)
    c: Block(g9)
    c: Coincident(g11,g8)
    c: Horizontal(g11)
    c: Block(g12)
    c: Block(g11)
    c: Coincident(g13,g12)
    c: Coincident(g13,g9)
    c: Vertical(g13)
    c: Tangent(g13,g9)
FEATURE [Sketcher::SketchObject] Sketch049
  FullyConstrained = true
  MapMode = 4
  Placement = pos=(0,0,0) rot=(0.57735,0.57735,0.57735;2.0944rad)
  Support = -> [Cut014]
  sketch-geometry (14):
    g0: LineSegment StartX=6.08745 StartY=-4.11588 StartZ=0 EndX=6.08745 EndY=-2.11589 EndZ=0
    g1: LineSegment StartX=8.08745 StartY=1.38411 StartZ=0 EndX=8.08745 EndY=-1.11589 EndZ=0
    g2: ArcOfCircle CenterX=7.08745 CenterY=-1.11589 CenterZ=0 NormalX=0 NormalY=0 NormalZ=1 AngleXU=0 Radius=1 StartAngle=4.71239 EndAngle=6.28319
    g3: LineSegment StartX=6.08745 StartY=-2.11589 StartZ=0 EndX=7.08745 EndY=-2.11589 EndZ=0
    g4: LineSegment StartX=6.08745 StartY=-4.11588 StartZ=0 EndX=7.08745 EndY=-4.11588 EndZ=0
    g5: ArcOfCircle CenterX=7.08745 CenterY=-1.11589 CenterZ=0 NormalX=0 NormalY=0 NormalZ=1 AngleXU=0 Radius=3 StartAngle=4.71239 EndAngle=6.28319
    g6: ArcOfCircle CenterX=7.08745 CenterY=1.38411 CenterZ=0 NormalX=0 NormalY=0 NormalZ=1 AngleXU=0 Radius=1 StartAngle=5.35e-14 EndAngle=1.5708
    g7: LineSegment StartX=10.0875 StartY=-1.11588 StartZ=0 EndX=10.0875 EndY=1.38411 EndZ=0
    g8: ArcOfCircle CenterX=7.08745 CenterY=1.38411 CenterZ=0 NormalX=0 NormalY=0 NormalZ=1 AngleXU=0 Radius=3 StartAngle=3.57e-14 EndAngle=1.5708
    g9: ArcOfCircle CenterX=4.58745 CenterY=1.38412 CenterZ=0 NormalX=0 NormalY=0 NormalZ=1 AngleXU=0 Radius=1 StartAngle=1.57081 EndAngle=3.14159
    g10: LineSegment StartX=4.58744 StartY=2.38411 StartZ=0 EndX=7.08745 EndY=2.38411 EndZ=0
    g11: LineSegment StartX=4.58745 StartY=4.38411 StartZ=0 EndX=7.08745 EndY=4.38411 EndZ=0
    g12: ArcOfCircle CenterX=4.58745 CenterY=5.38411 CenterZ=0 NormalX=0 NormalY=0 NormalZ=1 AngleXU=0 Radius=1 StartAngle=3.14159 EndAngle=4.71239
    g13: LineSegment StartX=3.58745 StartY=5.38411 StartZ=0 EndX=3.58745 EndY=1.38411 EndZ=0
  constraints (33):
    c: Vertical(g0)
    c: Block(g0)
    c: Block(g1)
    c: Coincident(g2,g1)
    c: Coincident(g3,g0)
    c: Coincident(g3,g2)
    c: Horizontal(g3)
    c: Block(g2)
    c: Coincident(g4,g0)
    c: Horizontal(g4)
    c: Coincident(g5,g2)
    c: Block(g5)
    c: Block(g4)
    c: Coincident(g6,g1)
    c: Block(g6)
    c: Coincident(g7,g5)
    c: Vertical(g7)
    c: Coincident(g8,g6)
    c: Block(g8)
    c: Block(g7)
    c: Coincident(g10,g9)
    c: Coincident(g10,g6)
    c: Horizontal(g10)
    c: Block(g10)
    c: Block(g9)
    c: Coincident(g11,g8)
    c: Horizontal(g11)
    c: Block(g12)
    c: Block(g11)
    c: Coincident(g13,g12)
    c: Coincident(g13,g9)
    c: Vertical(g13)
    c: Tangent(g13,g9)
FEATURE [Part::Extrusion] Extrude041
  Base = -> Sketch049
  Dir = (1,0,0)
  DirMode = 2
  FaceMakerClass = Part::FaceMakerBullseye
  LengthFwd = 10
  LengthRev = 0
  Placement = pos=(-2,-22.615,14.6) rot=(0,0,1;3.14159rad)
  Solid = true
  Symmetric = false
